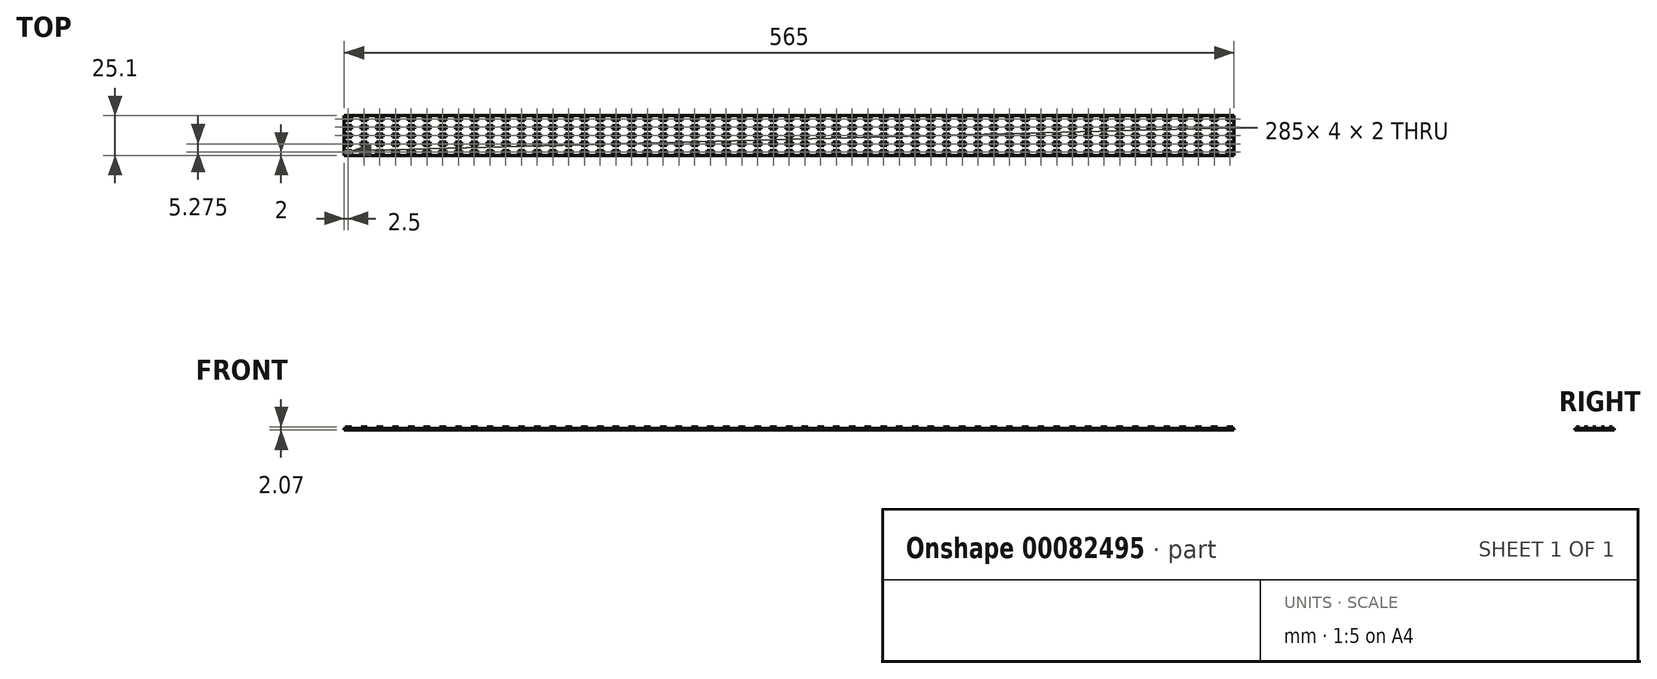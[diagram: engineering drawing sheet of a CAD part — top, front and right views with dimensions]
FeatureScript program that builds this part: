
annotation { "Feature Type Name" : "Feature", "Feature Type Description" : "" }
export const myFeature = defineFeature(function(context is Context, id is Id, definition is map)
    precondition{}
    {
        {
            var Q0;
            Q0=qCreatedBy(makeId("Right.planeOp"),FACE);
            var sketch = newSketch(context, id + "F0", { "sketchPlane" : qUnion([Q0])});
            skArc(sketch, "E0", {"start": v(-12.55, 0) * mm, "mid": v(0, -12.55) * mm, "end": v(12.55, 0) * mm});
            skLineSegment(sketch, "E1", {"start": v(-12.55, 0) * mm, "end": v(12.55, 0) * mm});
            skSolve(sketch);
        }
        {
            var Q0;
            Q0=qSketchRegion(id+"F0",true);
            extrude(context, id + "F1", {"entities" : qUnion([Q0]), "endBound" : BoundingType.SYMMETRIC, "depth" : 565 * mm});
        }
        {
            var Q0;
            Q0=makeQuery(id+"F1.opExtrude","SWEPT_FACE",FACE,{"disambiguationData":[OSD([sQuery(id+"F0.wireOp",EDGE,"E1")])]});
            var sketch = newSketch(context, id + "F2", { "sketchPlane" : qUnion([Q0])});
            skLineSegment(sketch, "E2.bottom", {"start": v(-282, 11.55) * mm, "end": v(-278, 11.55) * mm});
            skLineSegment(sketch, "E2.top", {"start": v(-282, 9.55) * mm, "end": v(-278, 9.55) * mm});
            skLineSegment(sketch, "E2.left", {"start": v(-282, 11.55) * mm, "end": v(-282, 9.55) * mm});
            skLineSegment(sketch, "E2.right", {"start": v(-278, 11.55) * mm, "end": v(-278, 9.55) * mm});
            skLineSegment(sketch, "E3.1.0.0", {"start": v(-282, 6.27) * mm, "end": v(-282, 4.27) * mm});
            skLineSegment(sketch, "E3.1.0.1", {"start": v(-282, 6.27) * mm, "end": v(-278, 6.27) * mm});
            skLineSegment(sketch, "E3.1.0.2", {"start": v(-278, 6.27) * mm, "end": v(-278, 4.27) * mm});
            skLineSegment(sketch, "E3.1.0.3", {"start": v(-282, 4.27) * mm, "end": v(-278, 4.27) * mm});
            skLineSegment(sketch, "E3.2.0.0", {"start": v(-282, 1) * mm, "end": v(-282, -1) * mm});
            skLineSegment(sketch, "E3.2.0.1", {"start": v(-282, 1) * mm, "end": v(-278, 1) * mm});
            skLineSegment(sketch, "E3.2.0.2", {"start": v(-278, 1) * mm, "end": v(-278, -1) * mm});
            skLineSegment(sketch, "E3.2.0.3", {"start": v(-282, -1) * mm, "end": v(-278, -1) * mm});
            skLineSegment(sketch, "E3.direction1", {"start": v(-278, 9.55) * mm, "end": v(-278, 4.27) * mm, "construction": true});
            skLineSegment(sketch, "E4.0.3.0", {"start": v(-282, -4.28) * mm, "end": v(-282, -6.28) * mm});
            skLineSegment(sketch, "E4.3.3.0", {"start": v(-282, -4.28) * mm, "end": v(-278, -4.28) * mm});
            skLineSegment(sketch, "E4.6.3.0", {"start": v(-278, -4.28) * mm, "end": v(-278, -6.28) * mm});
            skLineSegment(sketch, "E4.9.3.0", {"start": v(-282, -6.28) * mm, "end": v(-278, -6.28) * mm});
            skLineSegment(sketch, "E5.0.4.0", {"start": v(-282, -9.55) * mm, "end": v(-282, -11.55) * mm});
            skLineSegment(sketch, "E5.3.4.0", {"start": v(-282, -9.55) * mm, "end": v(-278, -9.55) * mm});
            skLineSegment(sketch, "E5.6.4.0", {"start": v(-278, -9.55) * mm, "end": v(-278, -11.55) * mm});
            skLineSegment(sketch, "E5.9.4.0", {"start": v(-282, -11.55) * mm, "end": v(-278, -11.55) * mm});
            skLineSegment(sketch, "E6.1.0.0", {"start": v(-272, -9.55) * mm, "end": v(-272, -11.55) * mm});
            skLineSegment(sketch, "E6.1.0.1", {"start": v(-268, -9.55) * mm, "end": v(-268, -11.55) * mm});
            skLineSegment(sketch, "E6.1.0.2", {"start": v(-272, -9.55) * mm, "end": v(-268, -9.55) * mm});
            skLineSegment(sketch, "E6.1.0.3", {"start": v(-268, 9.55) * mm, "end": v(-268, 4.27) * mm, "construction": true});
            skLineSegment(sketch, "E6.1.0.4", {"start": v(-272, -1) * mm, "end": v(-268, -1) * mm});
            skLineSegment(sketch, "E6.1.0.5", {"start": v(-272, -11.55) * mm, "end": v(-268, -11.55) * mm});
            skLineSegment(sketch, "E6.1.0.6", {"start": v(-268, 1) * mm, "end": v(-268, -1) * mm});
            skLineSegment(sketch, "E6.1.0.7", {"start": v(-272, 1) * mm, "end": v(-268, 1) * mm});
            skLineSegment(sketch, "E6.1.0.8", {"start": v(-272, 1) * mm, "end": v(-272, -1) * mm});
            skLineSegment(sketch, "E6.1.0.9", {"start": v(-272, 4.27) * mm, "end": v(-268, 4.27) * mm});
            skLineSegment(sketch, "E6.1.0.10", {"start": v(-268, 6.27) * mm, "end": v(-268, 4.27) * mm});
            skLineSegment(sketch, "E6.1.0.11", {"start": v(-272, 6.27) * mm, "end": v(-268, 6.27) * mm});
            skLineSegment(sketch, "E6.1.0.12", {"start": v(-272, 6.27) * mm, "end": v(-272, 4.27) * mm});
            skLineSegment(sketch, "E6.1.0.13", {"start": v(-268, 11.55) * mm, "end": v(-268, 9.55) * mm});
            skLineSegment(sketch, "E6.1.0.14", {"start": v(-272, 11.55) * mm, "end": v(-272, 9.55) * mm});
            skLineSegment(sketch, "E6.1.0.15", {"start": v(-272, 9.55) * mm, "end": v(-268, 9.55) * mm});
            skLineSegment(sketch, "E6.1.0.16", {"start": v(-272, -6.28) * mm, "end": v(-268, -6.28) * mm});
            skLineSegment(sketch, "E6.1.0.17", {"start": v(-272, 11.55) * mm, "end": v(-268, 11.55) * mm});
            skLineSegment(sketch, "E6.1.0.18", {"start": v(-268, -4.28) * mm, "end": v(-268, -6.28) * mm});
            skLineSegment(sketch, "E6.1.0.19", {"start": v(-272, -4.28) * mm, "end": v(-268, -4.28) * mm});
            skLineSegment(sketch, "E6.1.0.20", {"start": v(-272, -4.28) * mm, "end": v(-272, -6.28) * mm});
            skLineSegment(sketch, "E6.2.0.0", {"start": v(-262, -9.55) * mm, "end": v(-262, -11.55) * mm});
            skLineSegment(sketch, "E6.2.0.1", {"start": v(-258, -9.55) * mm, "end": v(-258, -11.55) * mm});
            skLineSegment(sketch, "E6.2.0.2", {"start": v(-262, -9.55) * mm, "end": v(-258, -9.55) * mm});
            skLineSegment(sketch, "E6.2.0.3", {"start": v(-258, 9.55) * mm, "end": v(-258, 4.27) * mm, "construction": true});
            skLineSegment(sketch, "E6.2.0.4", {"start": v(-262, -1) * mm, "end": v(-258, -1) * mm});
            skLineSegment(sketch, "E6.2.0.5", {"start": v(-262, -11.55) * mm, "end": v(-258, -11.55) * mm});
            skLineSegment(sketch, "E6.2.0.6", {"start": v(-258, 1) * mm, "end": v(-258, -1) * mm});
            skLineSegment(sketch, "E6.2.0.7", {"start": v(-262, 1) * mm, "end": v(-258, 1) * mm});
            skLineSegment(sketch, "E6.2.0.8", {"start": v(-262, 1) * mm, "end": v(-262, -1) * mm});
            skLineSegment(sketch, "E6.2.0.9", {"start": v(-262, 4.27) * mm, "end": v(-258, 4.27) * mm});
            skLineSegment(sketch, "E6.2.0.10", {"start": v(-258, 6.27) * mm, "end": v(-258, 4.27) * mm});
            skLineSegment(sketch, "E6.2.0.11", {"start": v(-262, 6.27) * mm, "end": v(-258, 6.27) * mm});
            skLineSegment(sketch, "E6.2.0.12", {"start": v(-262, 6.27) * mm, "end": v(-262, 4.27) * mm});
            skLineSegment(sketch, "E6.2.0.13", {"start": v(-258, 11.55) * mm, "end": v(-258, 9.55) * mm});
            skLineSegment(sketch, "E6.2.0.14", {"start": v(-262, 11.55) * mm, "end": v(-262, 9.55) * mm});
            skLineSegment(sketch, "E6.2.0.15", {"start": v(-262, 9.55) * mm, "end": v(-258, 9.55) * mm});
            skLineSegment(sketch, "E6.2.0.16", {"start": v(-262, -6.28) * mm, "end": v(-258, -6.28) * mm});
            skLineSegment(sketch, "E6.2.0.17", {"start": v(-262, 11.55) * mm, "end": v(-258, 11.55) * mm});
            skLineSegment(sketch, "E6.2.0.18", {"start": v(-258, -4.28) * mm, "end": v(-258, -6.28) * mm});
            skLineSegment(sketch, "E6.2.0.19", {"start": v(-262, -4.28) * mm, "end": v(-258, -4.28) * mm});
            skLineSegment(sketch, "E6.2.0.20", {"start": v(-262, -4.28) * mm, "end": v(-262, -6.28) * mm});
            skLineSegment(sketch, "E6.3.0.0", {"start": v(-252, -9.55) * mm, "end": v(-252, -11.55) * mm});
            skLineSegment(sketch, "E6.3.0.1", {"start": v(-248, -9.55) * mm, "end": v(-248, -11.55) * mm});
            skLineSegment(sketch, "E6.3.0.2", {"start": v(-252, -9.55) * mm, "end": v(-248, -9.55) * mm});
            skLineSegment(sketch, "E6.3.0.3", {"start": v(-248, 9.55) * mm, "end": v(-248, 4.27) * mm, "construction": true});
            skLineSegment(sketch, "E6.3.0.4", {"start": v(-252, -1) * mm, "end": v(-248, -1) * mm});
            skLineSegment(sketch, "E6.3.0.5", {"start": v(-252, -11.55) * mm, "end": v(-248, -11.55) * mm});
            skLineSegment(sketch, "E6.3.0.6", {"start": v(-248, 1) * mm, "end": v(-248, -1) * mm});
            skLineSegment(sketch, "E6.3.0.7", {"start": v(-252, 1) * mm, "end": v(-248, 1) * mm});
            skLineSegment(sketch, "E6.3.0.8", {"start": v(-252, 1) * mm, "end": v(-252, -1) * mm});
            skLineSegment(sketch, "E6.3.0.9", {"start": v(-252, 4.27) * mm, "end": v(-248, 4.27) * mm});
            skLineSegment(sketch, "E6.3.0.10", {"start": v(-248, 6.27) * mm, "end": v(-248, 4.27) * mm});
            skLineSegment(sketch, "E6.3.0.11", {"start": v(-252, 6.27) * mm, "end": v(-248, 6.27) * mm});
            skLineSegment(sketch, "E6.3.0.12", {"start": v(-252, 6.27) * mm, "end": v(-252, 4.27) * mm});
            skLineSegment(sketch, "E6.3.0.13", {"start": v(-248, 11.55) * mm, "end": v(-248, 9.55) * mm});
            skLineSegment(sketch, "E6.3.0.14", {"start": v(-252, 11.55) * mm, "end": v(-252, 9.55) * mm});
            skLineSegment(sketch, "E6.3.0.15", {"start": v(-252, 9.55) * mm, "end": v(-248, 9.55) * mm});
            skLineSegment(sketch, "E6.3.0.16", {"start": v(-252, -6.28) * mm, "end": v(-248, -6.28) * mm});
            skLineSegment(sketch, "E6.3.0.17", {"start": v(-252, 11.55) * mm, "end": v(-248, 11.55) * mm});
            skLineSegment(sketch, "E6.3.0.18", {"start": v(-248, -4.28) * mm, "end": v(-248, -6.28) * mm});
            skLineSegment(sketch, "E6.3.0.19", {"start": v(-252, -4.28) * mm, "end": v(-248, -4.28) * mm});
            skLineSegment(sketch, "E6.3.0.20", {"start": v(-252, -4.28) * mm, "end": v(-252, -6.28) * mm});
            skLineSegment(sketch, "E6.4.0.0", {"start": v(-242, -9.55) * mm, "end": v(-242, -11.55) * mm});
            skLineSegment(sketch, "E6.4.0.1", {"start": v(-238, -9.55) * mm, "end": v(-238, -11.55) * mm});
            skLineSegment(sketch, "E6.4.0.2", {"start": v(-242, -9.55) * mm, "end": v(-238, -9.55) * mm});
            skLineSegment(sketch, "E6.4.0.3", {"start": v(-238, 9.55) * mm, "end": v(-238, 4.27) * mm, "construction": true});
            skLineSegment(sketch, "E6.4.0.4", {"start": v(-242, -1) * mm, "end": v(-238, -1) * mm});
            skLineSegment(sketch, "E6.4.0.5", {"start": v(-242, -11.55) * mm, "end": v(-238, -11.55) * mm});
            skLineSegment(sketch, "E6.4.0.6", {"start": v(-238, 1) * mm, "end": v(-238, -1) * mm});
            skLineSegment(sketch, "E6.4.0.7", {"start": v(-242, 1) * mm, "end": v(-238, 1) * mm});
            skLineSegment(sketch, "E6.4.0.8", {"start": v(-242, 1) * mm, "end": v(-242, -1) * mm});
            skLineSegment(sketch, "E6.4.0.9", {"start": v(-242, 4.27) * mm, "end": v(-238, 4.27) * mm});
            skLineSegment(sketch, "E6.4.0.10", {"start": v(-238, 6.27) * mm, "end": v(-238, 4.27) * mm});
            skLineSegment(sketch, "E6.4.0.11", {"start": v(-242, 6.27) * mm, "end": v(-238, 6.27) * mm});
            skLineSegment(sketch, "E6.4.0.12", {"start": v(-242, 6.27) * mm, "end": v(-242, 4.27) * mm});
            skLineSegment(sketch, "E6.4.0.13", {"start": v(-238, 11.55) * mm, "end": v(-238, 9.55) * mm});
            skLineSegment(sketch, "E6.4.0.14", {"start": v(-242, 11.55) * mm, "end": v(-242, 9.55) * mm});
            skLineSegment(sketch, "E6.4.0.15", {"start": v(-242, 9.55) * mm, "end": v(-238, 9.55) * mm});
            skLineSegment(sketch, "E6.4.0.16", {"start": v(-242, -6.28) * mm, "end": v(-238, -6.28) * mm});
            skLineSegment(sketch, "E6.4.0.17", {"start": v(-242, 11.55) * mm, "end": v(-238, 11.55) * mm});
            skLineSegment(sketch, "E6.4.0.18", {"start": v(-238, -4.28) * mm, "end": v(-238, -6.28) * mm});
            skLineSegment(sketch, "E6.4.0.19", {"start": v(-242, -4.28) * mm, "end": v(-238, -4.28) * mm});
            skLineSegment(sketch, "E6.4.0.20", {"start": v(-242, -4.28) * mm, "end": v(-242, -6.28) * mm});
            skLineSegment(sketch, "E6.5.0.0", {"start": v(-232, -9.55) * mm, "end": v(-232, -11.55) * mm});
            skLineSegment(sketch, "E6.5.0.1", {"start": v(-228, -9.55) * mm, "end": v(-228, -11.55) * mm});
            skLineSegment(sketch, "E6.5.0.2", {"start": v(-232, -9.55) * mm, "end": v(-228, -9.55) * mm});
            skLineSegment(sketch, "E6.5.0.3", {"start": v(-228, 9.55) * mm, "end": v(-228, 4.27) * mm, "construction": true});
            skLineSegment(sketch, "E6.5.0.4", {"start": v(-232, -1) * mm, "end": v(-228, -1) * mm});
            skLineSegment(sketch, "E6.5.0.5", {"start": v(-232, -11.55) * mm, "end": v(-228, -11.55) * mm});
            skLineSegment(sketch, "E6.5.0.6", {"start": v(-228, 1) * mm, "end": v(-228, -1) * mm});
            skLineSegment(sketch, "E6.5.0.7", {"start": v(-232, 1) * mm, "end": v(-228, 1) * mm});
            skLineSegment(sketch, "E6.5.0.8", {"start": v(-232, 1) * mm, "end": v(-232, -1) * mm});
            skLineSegment(sketch, "E6.5.0.9", {"start": v(-232, 4.27) * mm, "end": v(-228, 4.27) * mm});
            skLineSegment(sketch, "E6.5.0.10", {"start": v(-228, 6.27) * mm, "end": v(-228, 4.27) * mm});
            skLineSegment(sketch, "E6.5.0.11", {"start": v(-232, 6.27) * mm, "end": v(-228, 6.27) * mm});
            skLineSegment(sketch, "E6.5.0.12", {"start": v(-232, 6.27) * mm, "end": v(-232, 4.27) * mm});
            skLineSegment(sketch, "E6.5.0.13", {"start": v(-228, 11.55) * mm, "end": v(-228, 9.55) * mm});
            skLineSegment(sketch, "E6.5.0.14", {"start": v(-232, 11.55) * mm, "end": v(-232, 9.55) * mm});
            skLineSegment(sketch, "E6.5.0.15", {"start": v(-232, 9.55) * mm, "end": v(-228, 9.55) * mm});
            skLineSegment(sketch, "E6.5.0.16", {"start": v(-232, -6.28) * mm, "end": v(-228, -6.28) * mm});
            skLineSegment(sketch, "E6.5.0.17", {"start": v(-232, 11.55) * mm, "end": v(-228, 11.55) * mm});
            skLineSegment(sketch, "E6.5.0.18", {"start": v(-228, -4.28) * mm, "end": v(-228, -6.28) * mm});
            skLineSegment(sketch, "E6.5.0.19", {"start": v(-232, -4.28) * mm, "end": v(-228, -4.28) * mm});
            skLineSegment(sketch, "E6.5.0.20", {"start": v(-232, -4.28) * mm, "end": v(-232, -6.28) * mm});
            skLineSegment(sketch, "E6.6.0.0", {"start": v(-222, -9.55) * mm, "end": v(-222, -11.55) * mm});
            skLineSegment(sketch, "E6.6.0.1", {"start": v(-218, -9.55) * mm, "end": v(-218, -11.55) * mm});
            skLineSegment(sketch, "E6.6.0.2", {"start": v(-222, -9.55) * mm, "end": v(-218, -9.55) * mm});
            skLineSegment(sketch, "E6.6.0.3", {"start": v(-218, 9.55) * mm, "end": v(-218, 4.27) * mm, "construction": true});
            skLineSegment(sketch, "E6.6.0.4", {"start": v(-222, -1) * mm, "end": v(-218, -1) * mm});
            skLineSegment(sketch, "E6.6.0.5", {"start": v(-222, -11.55) * mm, "end": v(-218, -11.55) * mm});
            skLineSegment(sketch, "E6.6.0.6", {"start": v(-218, 1) * mm, "end": v(-218, -1) * mm});
            skLineSegment(sketch, "E6.6.0.7", {"start": v(-222, 1) * mm, "end": v(-218, 1) * mm});
            skLineSegment(sketch, "E6.6.0.8", {"start": v(-222, 1) * mm, "end": v(-222, -1) * mm});
            skLineSegment(sketch, "E6.6.0.9", {"start": v(-222, 4.27) * mm, "end": v(-218, 4.27) * mm});
            skLineSegment(sketch, "E6.6.0.10", {"start": v(-218, 6.27) * mm, "end": v(-218, 4.27) * mm});
            skLineSegment(sketch, "E6.6.0.11", {"start": v(-222, 6.27) * mm, "end": v(-218, 6.27) * mm});
            skLineSegment(sketch, "E6.6.0.12", {"start": v(-222, 6.27) * mm, "end": v(-222, 4.27) * mm});
            skLineSegment(sketch, "E6.6.0.13", {"start": v(-218, 11.55) * mm, "end": v(-218, 9.55) * mm});
            skLineSegment(sketch, "E6.6.0.14", {"start": v(-222, 11.55) * mm, "end": v(-222, 9.55) * mm});
            skLineSegment(sketch, "E6.6.0.15", {"start": v(-222, 9.55) * mm, "end": v(-218, 9.55) * mm});
            skLineSegment(sketch, "E6.6.0.16", {"start": v(-222, -6.28) * mm, "end": v(-218, -6.28) * mm});
            skLineSegment(sketch, "E6.6.0.17", {"start": v(-222, 11.55) * mm, "end": v(-218, 11.55) * mm});
            skLineSegment(sketch, "E6.6.0.18", {"start": v(-218, -4.28) * mm, "end": v(-218, -6.28) * mm});
            skLineSegment(sketch, "E6.6.0.19", {"start": v(-222, -4.28) * mm, "end": v(-218, -4.28) * mm});
            skLineSegment(sketch, "E6.6.0.20", {"start": v(-222, -4.28) * mm, "end": v(-222, -6.28) * mm});
            skLineSegment(sketch, "E6.7.0.0", {"start": v(-212, -9.55) * mm, "end": v(-212, -11.55) * mm});
            skLineSegment(sketch, "E6.7.0.1", {"start": v(-208, -9.55) * mm, "end": v(-208, -11.55) * mm});
            skLineSegment(sketch, "E6.7.0.2", {"start": v(-212, -9.55) * mm, "end": v(-208, -9.55) * mm});
            skLineSegment(sketch, "E6.7.0.3", {"start": v(-208, 9.55) * mm, "end": v(-208, 4.27) * mm, "construction": true});
            skLineSegment(sketch, "E6.7.0.4", {"start": v(-212, -1) * mm, "end": v(-208, -1) * mm});
            skLineSegment(sketch, "E6.7.0.5", {"start": v(-212, -11.55) * mm, "end": v(-208, -11.55) * mm});
            skLineSegment(sketch, "E6.7.0.6", {"start": v(-208, 1) * mm, "end": v(-208, -1) * mm});
            skLineSegment(sketch, "E6.7.0.7", {"start": v(-212, 1) * mm, "end": v(-208, 1) * mm});
            skLineSegment(sketch, "E6.7.0.8", {"start": v(-212, 1) * mm, "end": v(-212, -1) * mm});
            skLineSegment(sketch, "E6.7.0.9", {"start": v(-212, 4.27) * mm, "end": v(-208, 4.27) * mm});
            skLineSegment(sketch, "E6.7.0.10", {"start": v(-208, 6.27) * mm, "end": v(-208, 4.27) * mm});
            skLineSegment(sketch, "E6.7.0.11", {"start": v(-212, 6.27) * mm, "end": v(-208, 6.27) * mm});
            skLineSegment(sketch, "E6.7.0.12", {"start": v(-212, 6.27) * mm, "end": v(-212, 4.27) * mm});
            skLineSegment(sketch, "E6.7.0.13", {"start": v(-208, 11.55) * mm, "end": v(-208, 9.55) * mm});
            skLineSegment(sketch, "E6.7.0.14", {"start": v(-212, 11.55) * mm, "end": v(-212, 9.55) * mm});
            skLineSegment(sketch, "E6.7.0.15", {"start": v(-212, 9.55) * mm, "end": v(-208, 9.55) * mm});
            skLineSegment(sketch, "E6.7.0.16", {"start": v(-212, -6.28) * mm, "end": v(-208, -6.28) * mm});
            skLineSegment(sketch, "E6.7.0.17", {"start": v(-212, 11.55) * mm, "end": v(-208, 11.55) * mm});
            skLineSegment(sketch, "E6.7.0.18", {"start": v(-208, -4.28) * mm, "end": v(-208, -6.28) * mm});
            skLineSegment(sketch, "E6.7.0.19", {"start": v(-212, -4.28) * mm, "end": v(-208, -4.28) * mm});
            skLineSegment(sketch, "E6.7.0.20", {"start": v(-212, -4.28) * mm, "end": v(-212, -6.28) * mm});
            skLineSegment(sketch, "E6.8.0.0", {"start": v(-202, -9.55) * mm, "end": v(-202, -11.55) * mm});
            skLineSegment(sketch, "E6.8.0.1", {"start": v(-198, -9.55) * mm, "end": v(-198, -11.55) * mm});
            skLineSegment(sketch, "E6.8.0.2", {"start": v(-202, -9.55) * mm, "end": v(-198, -9.55) * mm});
            skLineSegment(sketch, "E6.8.0.3", {"start": v(-198, 9.55) * mm, "end": v(-198, 4.27) * mm, "construction": true});
            skLineSegment(sketch, "E6.8.0.4", {"start": v(-202, -1) * mm, "end": v(-198, -1) * mm});
            skLineSegment(sketch, "E6.8.0.5", {"start": v(-202, -11.55) * mm, "end": v(-198, -11.55) * mm});
            skLineSegment(sketch, "E6.8.0.6", {"start": v(-198, 1) * mm, "end": v(-198, -1) * mm});
            skLineSegment(sketch, "E6.8.0.7", {"start": v(-202, 1) * mm, "end": v(-198, 1) * mm});
            skLineSegment(sketch, "E6.8.0.8", {"start": v(-202, 1) * mm, "end": v(-202, -1) * mm});
            skLineSegment(sketch, "E6.8.0.9", {"start": v(-202, 4.27) * mm, "end": v(-198, 4.27) * mm});
            skLineSegment(sketch, "E6.8.0.10", {"start": v(-198, 6.27) * mm, "end": v(-198, 4.27) * mm});
            skLineSegment(sketch, "E6.8.0.11", {"start": v(-202, 6.27) * mm, "end": v(-198, 6.27) * mm});
            skLineSegment(sketch, "E6.8.0.12", {"start": v(-202, 6.27) * mm, "end": v(-202, 4.27) * mm});
            skLineSegment(sketch, "E6.8.0.13", {"start": v(-198, 11.55) * mm, "end": v(-198, 9.55) * mm});
            skLineSegment(sketch, "E6.8.0.14", {"start": v(-202, 11.55) * mm, "end": v(-202, 9.55) * mm});
            skLineSegment(sketch, "E6.8.0.15", {"start": v(-202, 9.55) * mm, "end": v(-198, 9.55) * mm});
            skLineSegment(sketch, "E6.8.0.16", {"start": v(-202, -6.28) * mm, "end": v(-198, -6.28) * mm});
            skLineSegment(sketch, "E6.8.0.17", {"start": v(-202, 11.55) * mm, "end": v(-198, 11.55) * mm});
            skLineSegment(sketch, "E6.8.0.18", {"start": v(-198, -4.28) * mm, "end": v(-198, -6.28) * mm});
            skLineSegment(sketch, "E6.8.0.19", {"start": v(-202, -4.28) * mm, "end": v(-198, -4.28) * mm});
            skLineSegment(sketch, "E6.8.0.20", {"start": v(-202, -4.28) * mm, "end": v(-202, -6.28) * mm});
            skLineSegment(sketch, "E6.9.0.0", {"start": v(-192, -9.55) * mm, "end": v(-192, -11.55) * mm});
            skLineSegment(sketch, "E6.9.0.1", {"start": v(-188, -9.55) * mm, "end": v(-188, -11.55) * mm});
            skLineSegment(sketch, "E6.9.0.2", {"start": v(-192, -9.55) * mm, "end": v(-188, -9.55) * mm});
            skLineSegment(sketch, "E6.9.0.3", {"start": v(-188, 9.55) * mm, "end": v(-188, 4.27) * mm, "construction": true});
            skLineSegment(sketch, "E6.9.0.4", {"start": v(-192, -1) * mm, "end": v(-188, -1) * mm});
            skLineSegment(sketch, "E6.9.0.5", {"start": v(-192, -11.55) * mm, "end": v(-188, -11.55) * mm});
            skLineSegment(sketch, "E6.9.0.6", {"start": v(-188, 1) * mm, "end": v(-188, -1) * mm});
            skLineSegment(sketch, "E6.9.0.7", {"start": v(-192, 1) * mm, "end": v(-188, 1) * mm});
            skLineSegment(sketch, "E6.9.0.8", {"start": v(-192, 1) * mm, "end": v(-192, -1) * mm});
            skLineSegment(sketch, "E6.9.0.9", {"start": v(-192, 4.27) * mm, "end": v(-188, 4.27) * mm});
            skLineSegment(sketch, "E6.9.0.10", {"start": v(-188, 6.27) * mm, "end": v(-188, 4.27) * mm});
            skLineSegment(sketch, "E6.9.0.11", {"start": v(-192, 6.27) * mm, "end": v(-188, 6.27) * mm});
            skLineSegment(sketch, "E6.9.0.12", {"start": v(-192, 6.27) * mm, "end": v(-192, 4.27) * mm});
            skLineSegment(sketch, "E6.9.0.13", {"start": v(-188, 11.55) * mm, "end": v(-188, 9.55) * mm});
            skLineSegment(sketch, "E6.9.0.14", {"start": v(-192, 11.55) * mm, "end": v(-192, 9.55) * mm});
            skLineSegment(sketch, "E6.9.0.15", {"start": v(-192, 9.55) * mm, "end": v(-188, 9.55) * mm});
            skLineSegment(sketch, "E6.9.0.16", {"start": v(-192, -6.28) * mm, "end": v(-188, -6.28) * mm});
            skLineSegment(sketch, "E6.9.0.17", {"start": v(-192, 11.55) * mm, "end": v(-188, 11.55) * mm});
            skLineSegment(sketch, "E6.9.0.18", {"start": v(-188, -4.28) * mm, "end": v(-188, -6.28) * mm});
            skLineSegment(sketch, "E6.9.0.19", {"start": v(-192, -4.28) * mm, "end": v(-188, -4.28) * mm});
            skLineSegment(sketch, "E6.9.0.20", {"start": v(-192, -4.28) * mm, "end": v(-192, -6.28) * mm});
            skLineSegment(sketch, "E6.direction1", {"start": v(-282, -11.55) * mm, "end": v(-272, -11.55) * mm, "construction": true});
            skLineSegment(sketch, "E7.1.0.0", {"start": v(-172, -9.55) * mm, "end": v(-168, -9.55) * mm});
            skLineSegment(sketch, "E7.1.0.1", {"start": v(-168, -9.55) * mm, "end": v(-168, -11.55) * mm});
            skLineSegment(sketch, "E7.1.0.2", {"start": v(-102, 11.55) * mm, "end": v(-102, 9.55) * mm});
            skLineSegment(sketch, "E7.1.0.3", {"start": v(-112, -1) * mm, "end": v(-108, -1) * mm});
            skLineSegment(sketch, "E7.1.0.4", {"start": v(-132, 11.55) * mm, "end": v(-132, 9.55) * mm});
            skLineSegment(sketch, "E7.1.0.5", {"start": v(-102, 9.55) * mm, "end": v(-98, 9.55) * mm});
            skLineSegment(sketch, "E7.1.0.6", {"start": v(-162, 11.55) * mm, "end": v(-162, 9.55) * mm});
            skLineSegment(sketch, "E7.1.0.7", {"start": v(-132, 9.55) * mm, "end": v(-128, 9.55) * mm});
            skLineSegment(sketch, "E7.1.0.8", {"start": v(-102, -9.55) * mm, "end": v(-102, -11.55) * mm});
            skLineSegment(sketch, "E7.1.0.9", {"start": v(-162, 9.55) * mm, "end": v(-158, 9.55) * mm});
            skLineSegment(sketch, "E7.1.0.10", {"start": v(-108, 1) * mm, "end": v(-108, -1) * mm});
            skLineSegment(sketch, "E7.1.0.11", {"start": v(-92, 6.27) * mm, "end": v(-92, 4.27) * mm});
            skLineSegment(sketch, "E7.1.0.12", {"start": v(-102, 11.55) * mm, "end": v(-98, 11.55) * mm});
            skLineSegment(sketch, "E7.1.0.13", {"start": v(-98, -9.55) * mm, "end": v(-98, -11.55) * mm});
            skLineSegment(sketch, "E7.1.0.14", {"start": v(-172, -11.55) * mm, "end": v(-168, -11.55) * mm});
            skLineSegment(sketch, "E7.1.0.15", {"start": v(-112, 1) * mm, "end": v(-108, 1) * mm});
            skLineSegment(sketch, "E7.1.0.16", {"start": v(-132, 11.55) * mm, "end": v(-128, 11.55) * mm});
            skLineSegment(sketch, "E7.1.0.17", {"start": v(-128, -9.55) * mm, "end": v(-128, -11.55) * mm});
            skLineSegment(sketch, "E7.1.0.18", {"start": v(-102, -9.55) * mm, "end": v(-98, -9.55) * mm});
            skLineSegment(sketch, "E7.1.0.19", {"start": v(-162, 11.55) * mm, "end": v(-158, 11.55) * mm});
            skLineSegment(sketch, "E7.1.0.20", {"start": v(-132, -9.55) * mm, "end": v(-128, -9.55) * mm});
            skLineSegment(sketch, "E7.1.0.21", {"start": v(-132, -1) * mm, "end": v(-128, -1) * mm});
            skLineSegment(sketch, "E7.1.0.22", {"start": v(-102, -11.55) * mm, "end": v(-98, -11.55) * mm});
            skLineSegment(sketch, "E7.1.0.23", {"start": v(-162, -1) * mm, "end": v(-158, -1) * mm});
            skLineSegment(sketch, "E7.1.0.24", {"start": v(-132, -11.55) * mm, "end": v(-128, -11.55) * mm});
            skLineSegment(sketch, "E7.1.0.25", {"start": v(-122, -9.55) * mm, "end": v(-122, -11.55) * mm});
            skLineSegment(sketch, "E7.1.0.26", {"start": v(-88, -9.55) * mm, "end": v(-88, -11.55) * mm});
            skLineSegment(sketch, "E7.1.0.27", {"start": v(-128, 1) * mm, "end": v(-128, -1) * mm});
            skLineSegment(sketch, "E7.1.0.28", {"start": v(-152, -9.55) * mm, "end": v(-152, -11.55) * mm});
            skLineSegment(sketch, "E7.1.0.29", {"start": v(-118, -9.55) * mm, "end": v(-118, -11.55) * mm});
            skLineSegment(sketch, "E7.1.0.30", {"start": v(-92, -9.55) * mm, "end": v(-88, -9.55) * mm});
            skLineSegment(sketch, "E7.1.0.31", {"start": v(-132, 1) * mm, "end": v(-128, 1) * mm});
            skLineSegment(sketch, "E7.1.0.32", {"start": v(-148, -9.55) * mm, "end": v(-148, -11.55) * mm});
            skLineSegment(sketch, "E7.1.0.33", {"start": v(-122, -9.55) * mm, "end": v(-118, -9.55) * mm});
            skLineSegment(sketch, "E7.1.0.34", {"start": v(-152, -9.55) * mm, "end": v(-148, -9.55) * mm});
            skLineSegment(sketch, "E7.1.0.35", {"start": v(-112, 11.55) * mm, "end": v(-112, 9.55) * mm});
            skLineSegment(sketch, "E7.1.0.36", {"start": v(-172, 6.27) * mm, "end": v(-172, 4.27) * mm});
            skLineSegment(sketch, "E7.1.0.37", {"start": v(-112, 9.55) * mm, "end": v(-108, 9.55) * mm});
            skLineSegment(sketch, "E7.1.0.38", {"start": v(-92, -11.55) * mm, "end": v(-88, -11.55) * mm});
            skLineSegment(sketch, "E7.1.0.39", {"start": v(-162, 1) * mm, "end": v(-162, -1) * mm});
            skLineSegment(sketch, "E7.1.0.40", {"start": v(-122, -11.55) * mm, "end": v(-118, -11.55) * mm});
            skLineSegment(sketch, "E7.1.0.41", {"start": v(-182, 11.55) * mm, "end": v(-178, 11.55) * mm});
            skLineSegment(sketch, "E7.1.0.42", {"start": v(-182, 9.55) * mm, "end": v(-178, 9.55) * mm});
            skLineSegment(sketch, "E7.1.0.43", {"start": v(-182, 11.55) * mm, "end": v(-182, 9.55) * mm});
            skLineSegment(sketch, "E7.1.0.44", {"start": v(-182, 6.27) * mm, "end": v(-182, 4.27) * mm});
            skLineSegment(sketch, "E7.1.0.45", {"start": v(-182, 6.27) * mm, "end": v(-178, 6.27) * mm});
            skLineSegment(sketch, "E7.1.0.46", {"start": v(-182, 4.27) * mm, "end": v(-178, 4.27) * mm});
            skLineSegment(sketch, "E7.1.0.47", {"start": v(-152, -11.55) * mm, "end": v(-148, -11.55) * mm});
            skLineSegment(sketch, "E7.1.0.48", {"start": v(-112, 11.55) * mm, "end": v(-108, 11.55) * mm});
            skLineSegment(sketch, "E7.1.0.49", {"start": v(-162, 6.27) * mm, "end": v(-162, 4.27) * mm});
            skLineSegment(sketch, "E7.1.0.50", {"start": v(-172, 11.55) * mm, "end": v(-168, 11.55) * mm});
            skLineSegment(sketch, "E7.1.0.51", {"start": v(-128, 11.55) * mm, "end": v(-128, 9.55) * mm});
            skLineSegment(sketch, "E7.1.0.52", {"start": v(-138, -4.28) * mm, "end": v(-138, -6.28) * mm});
            skLineSegment(sketch, "E7.1.0.53", {"start": v(-142, -9.55) * mm, "end": v(-138, -9.55) * mm});
            skLineSegment(sketch, "E7.1.0.54", {"start": v(-152, 1) * mm, "end": v(-148, 1) * mm});
            skLineSegment(sketch, "E7.1.0.55", {"start": v(-112, -4.28) * mm, "end": v(-108, -4.28) * mm});
            skLineSegment(sketch, "E7.1.0.56", {"start": v(-92, 4.27) * mm, "end": v(-88, 4.27) * mm});
            skLineSegment(sketch, "E7.1.0.57", {"start": v(-138, 9.55) * mm, "end": v(-138, 4.27) * mm, "construction": true});
            skLineSegment(sketch, "E7.1.0.58", {"start": v(-152, 1) * mm, "end": v(-152, -1) * mm});
            skLineSegment(sketch, "E7.1.0.59", {"start": v(-158, 11.55) * mm, "end": v(-158, 9.55) * mm});
            skLineSegment(sketch, "E7.1.0.60", {"start": v(-168, -4.28) * mm, "end": v(-168, -6.28) * mm});
            skLineSegment(sketch, "E7.1.0.61", {"start": v(-122, 4.27) * mm, "end": v(-118, 4.27) * mm});
            skLineSegment(sketch, "E7.1.0.62", {"start": v(-142, -4.28) * mm, "end": v(-138, -4.28) * mm});
            skLineSegment(sketch, "E7.1.0.63", {"start": v(-88, 6.27) * mm, "end": v(-88, 4.27) * mm});
            skLineSegment(sketch, "E7.1.0.64", {"start": v(-112, -4.28) * mm, "end": v(-112, -6.28) * mm});
            skLineSegment(sketch, "E7.1.0.65", {"start": v(-168, 9.55) * mm, "end": v(-168, 4.27) * mm, "construction": true});
            skLineSegment(sketch, "E7.1.0.66", {"start": v(-142, -1) * mm, "end": v(-138, -1) * mm});
            skLineSegment(sketch, "E7.1.0.67", {"start": v(-152, 4.27) * mm, "end": v(-148, 4.27) * mm});
            skLineSegment(sketch, "E7.1.0.68", {"start": v(-172, -4.28) * mm, "end": v(-168, -4.28) * mm});
            skLineSegment(sketch, "E7.1.0.69", {"start": v(-112, -11.55) * mm, "end": v(-108, -11.55) * mm});
            skLineSegment(sketch, "E7.1.0.70", {"start": v(-118, 6.27) * mm, "end": v(-118, 4.27) * mm});
            skLineSegment(sketch, "E7.1.0.71", {"start": v(-92, 6.27) * mm, "end": v(-88, 6.27) * mm});
            skLineSegment(sketch, "E7.1.0.72", {"start": v(-102, -6.28) * mm, "end": v(-98, -6.28) * mm});
            skLineSegment(sketch, "E7.1.0.73", {"start": v(-142, -11.55) * mm, "end": v(-138, -11.55) * mm});
            skLineSegment(sketch, "E7.1.0.74", {"start": v(-148, 6.27) * mm, "end": v(-148, 4.27) * mm});
            skLineSegment(sketch, "E7.1.0.75", {"start": v(-122, 6.27) * mm, "end": v(-118, 6.27) * mm});
            skLineSegment(sketch, "E7.1.0.76", {"start": v(-132, -6.28) * mm, "end": v(-128, -6.28) * mm});
            skLineSegment(sketch, "E7.1.0.77", {"start": v(-132, -9.55) * mm, "end": v(-132, -11.55) * mm});
            skLineSegment(sketch, "E7.1.0.78", {"start": v(-138, 1) * mm, "end": v(-138, -1) * mm});
            skLineSegment(sketch, "E7.1.0.79", {"start": v(-152, 6.27) * mm, "end": v(-148, 6.27) * mm});
            skLineSegment(sketch, "E7.1.0.80", {"start": v(-162, -6.28) * mm, "end": v(-158, -6.28) * mm});
            skLineSegment(sketch, "E7.1.0.81", {"start": v(-162, -9.55) * mm, "end": v(-162, -11.55) * mm});
            skLineSegment(sketch, "E7.1.0.82", {"start": v(-122, 6.27) * mm, "end": v(-122, 4.27) * mm});
            skLineSegment(sketch, "E7.1.0.83", {"start": v(-88, 11.55) * mm, "end": v(-88, 9.55) * mm});
            skLineSegment(sketch, "E7.1.0.84", {"start": v(-98, -4.28) * mm, "end": v(-98, -6.28) * mm});
            skLineSegment(sketch, "E7.1.0.85", {"start": v(-142, 1) * mm, "end": v(-138, 1) * mm});
            skLineSegment(sketch, "E7.1.0.86", {"start": v(-152, 6.27) * mm, "end": v(-152, 4.27) * mm});
            skLineSegment(sketch, "E7.1.0.87", {"start": v(-158, -9.55) * mm, "end": v(-158, -11.55) * mm});
            skLineSegment(sketch, "E7.1.0.88", {"start": v(-112, 1) * mm, "end": v(-112, -1) * mm});
            skLineSegment(sketch, "E7.1.0.89", {"start": v(-118, 11.55) * mm, "end": v(-118, 9.55) * mm});
            skLineSegment(sketch, "E7.1.0.90", {"start": v(-128, -4.28) * mm, "end": v(-128, -6.28) * mm});
            skLineSegment(sketch, "E7.1.0.91", {"start": v(-92, 11.55) * mm, "end": v(-92, 9.55) * mm});
            skLineSegment(sketch, "E7.1.0.92", {"start": v(-102, -4.28) * mm, "end": v(-98, -4.28) * mm});
            skLineSegment(sketch, "E7.1.0.93", {"start": v(-142, 4.27) * mm, "end": v(-138, 4.27) * mm});
            skLineSegment(sketch, "E7.1.0.94", {"start": v(-152, 11.55) * mm, "end": v(-152, 9.55) * mm});
            skLineSegment(sketch, "E7.1.0.95", {"start": v(-162, -4.28) * mm, "end": v(-158, -4.28) * mm});
            skLineSegment(sketch, "E7.1.0.96", {"start": v(-122, 9.55) * mm, "end": v(-118, 9.55) * mm});
            skLineSegment(sketch, "E7.1.0.97", {"start": v(-92, -6.28) * mm, "end": v(-88, -6.28) * mm});
            skLineSegment(sketch, "E7.1.0.98", {"start": v(-92, -9.55) * mm, "end": v(-92, -11.55) * mm});
            skLineSegment(sketch, "E7.1.0.99", {"start": v(-148, 11.55) * mm, "end": v(-148, 9.55) * mm});
            skLineSegment(sketch, "E7.1.0.100", {"start": v(-162, -9.55) * mm, "end": v(-158, -9.55) * mm});
            skLineSegment(sketch, "E7.1.0.101", {"start": v(-112, 4.27) * mm, "end": v(-108, 4.27) * mm});
            skLineSegment(sketch, "E7.1.0.102", {"start": v(-122, 11.55) * mm, "end": v(-122, 9.55) * mm});
            skLineSegment(sketch, "E7.1.0.103", {"start": v(-132, -4.28) * mm, "end": v(-128, -4.28) * mm});
            skLineSegment(sketch, "E7.1.0.104", {"start": v(-92, 9.55) * mm, "end": v(-88, 9.55) * mm});
            skLineSegment(sketch, "E7.1.0.105", {"start": v(-102, -1) * mm, "end": v(-98, -1) * mm});
            skLineSegment(sketch, "E7.1.0.106", {"start": v(-172, 4.27) * mm, "end": v(-168, 4.27) * mm});
            skLineSegment(sketch, "E7.1.0.107", {"start": v(-138, 6.27) * mm, "end": v(-138, 4.27) * mm});
            skLineSegment(sketch, "E7.1.0.108", {"start": v(-152, 9.55) * mm, "end": v(-148, 9.55) * mm});
            skLineSegment(sketch, "E7.1.0.109", {"start": v(-162, -4.28) * mm, "end": v(-162, -6.28) * mm});
            skLineSegment(sketch, "E7.1.0.110", {"start": v(-98, 1) * mm, "end": v(-98, -1) * mm});
            skLineSegment(sketch, "E7.1.0.111", {"start": v(-112, 6.27) * mm, "end": v(-108, 6.27) * mm});
            skLineSegment(sketch, "E7.1.0.112", {"start": v(-122, -6.28) * mm, "end": v(-118, -6.28) * mm});
            skLineSegment(sketch, "E7.1.0.113", {"start": v(-92, 11.55) * mm, "end": v(-88, 11.55) * mm});
            skLineSegment(sketch, "E7.1.0.114", {"start": v(-162, -11.55) * mm, "end": v(-158, -11.55) * mm});
            skLineSegment(sketch, "E7.1.0.115", {"start": v(-168, 6.27) * mm, "end": v(-168, 4.27) * mm});
            skLineSegment(sketch, "E7.1.0.116", {"start": v(-142, 6.27) * mm, "end": v(-138, 6.27) * mm});
            skLineSegment(sketch, "E7.1.0.117", {"start": v(-152, -6.28) * mm, "end": v(-148, -6.28) * mm});
            skLineSegment(sketch, "E7.1.0.118", {"start": v(-102, 1) * mm, "end": v(-98, 1) * mm});
            skLineSegment(sketch, "E7.1.0.119", {"start": v(-112, 6.27) * mm, "end": v(-112, 4.27) * mm});
            skLineSegment(sketch, "E7.1.0.120", {"start": v(-122, 11.55) * mm, "end": v(-118, 11.55) * mm});
            skLineSegment(sketch, "E7.1.0.121", {"start": v(-88, -4.28) * mm, "end": v(-88, -6.28) * mm});
            skLineSegment(sketch, "E7.1.0.122", {"start": v(-158, 1) * mm, "end": v(-158, -1) * mm});
            skLineSegment(sketch, "E7.1.0.123", {"start": v(-172, 6.27) * mm, "end": v(-168, 6.27) * mm});
            skLineSegment(sketch, "E7.1.0.124", {"start": v(-182, -6.28) * mm, "end": v(-178, -6.28) * mm});
            skLineSegment(sketch, "E7.1.0.125", {"start": v(-142, 6.27) * mm, "end": v(-142, 4.27) * mm});
            skLineSegment(sketch, "E7.1.0.126", {"start": v(-152, 11.55) * mm, "end": v(-148, 11.55) * mm});
            skLineSegment(sketch, "E7.1.0.127", {"start": v(-102, 1) * mm, "end": v(-102, -1) * mm});
            skLineSegment(sketch, "E7.1.0.128", {"start": v(-108, 11.55) * mm, "end": v(-108, 9.55) * mm});
            skLineSegment(sketch, "E7.1.0.129", {"start": v(-118, -4.28) * mm, "end": v(-118, -6.28) * mm});
            skLineSegment(sketch, "E7.1.0.130", {"start": v(-92, -4.28) * mm, "end": v(-88, -4.28) * mm});
            skLineSegment(sketch, "E7.1.0.131", {"start": v(-88, 9.55) * mm, "end": v(-88, 4.27) * mm, "construction": true});
            skLineSegment(sketch, "E7.1.0.132", {"start": v(-132, 1) * mm, "end": v(-132, -1) * mm});
            skLineSegment(sketch, "E7.1.0.133", {"start": v(-138, 11.55) * mm, "end": v(-138, 9.55) * mm});
            skLineSegment(sketch, "E7.1.0.134", {"start": v(-148, -4.28) * mm, "end": v(-148, -6.28) * mm});
            skLineSegment(sketch, "E7.1.0.135", {"start": v(-122, -4.28) * mm, "end": v(-118, -4.28) * mm});
            skLineSegment(sketch, "E7.1.0.136", {"start": v(-118, 9.55) * mm, "end": v(-118, 4.27) * mm, "construction": true});
            skLineSegment(sketch, "E7.1.0.137", {"start": v(-92, -4.28) * mm, "end": v(-92, -6.28) * mm});
            skLineSegment(sketch, "E7.1.0.138", {"start": v(-162, 1) * mm, "end": v(-158, 1) * mm});
            skLineSegment(sketch, "E7.1.0.139", {"start": v(-182, -9.55) * mm, "end": v(-182, -11.55) * mm});
            skLineSegment(sketch, "E7.1.0.140", {"start": v(-122, -4.28) * mm, "end": v(-122, -6.28) * mm});
            skLineSegment(sketch, "E7.1.0.141", {"start": v(-182, -11.55) * mm, "end": v(-172, -11.55) * mm, "construction": true});
            skLineSegment(sketch, "E7.1.0.142", {"start": v(-168, 11.55) * mm, "end": v(-168, 9.55) * mm});
            skLineSegment(sketch, "E7.1.0.143", {"start": v(-182, -9.55) * mm, "end": v(-178, -9.55) * mm});
            skLineSegment(sketch, "E7.1.0.144", {"start": v(-142, 11.55) * mm, "end": v(-142, 9.55) * mm});
            skLineSegment(sketch, "E7.1.0.145", {"start": v(-152, -4.28) * mm, "end": v(-148, -4.28) * mm});
            skLineSegment(sketch, "E7.1.0.146", {"start": v(-148, 9.55) * mm, "end": v(-148, 4.27) * mm, "construction": true});
            skLineSegment(sketch, "E7.1.0.147", {"start": v(-162, 4.27) * mm, "end": v(-158, 4.27) * mm});
            skLineSegment(sketch, "E7.1.0.148", {"start": v(-172, 11.55) * mm, "end": v(-172, 9.55) * mm});
            skLineSegment(sketch, "E7.1.0.149", {"start": v(-178, -9.55) * mm, "end": v(-178, -11.55) * mm});
            skLineSegment(sketch, "E7.1.0.150", {"start": v(-142, 9.55) * mm, "end": v(-138, 9.55) * mm});
            skLineSegment(sketch, "E7.1.0.151", {"start": v(-152, -4.28) * mm, "end": v(-152, -6.28) * mm});
            skLineSegment(sketch, "E7.1.0.152", {"start": v(-152, -1) * mm, "end": v(-148, -1) * mm});
            skLineSegment(sketch, "E7.1.0.153", {"start": v(-112, -6.28) * mm, "end": v(-108, -6.28) * mm});
            skLineSegment(sketch, "E7.1.0.154", {"start": v(-112, -9.55) * mm, "end": v(-112, -11.55) * mm});
            skLineSegment(sketch, "E7.1.0.155", {"start": v(-182, -4.28) * mm, "end": v(-182, -6.28) * mm});
            skLineSegment(sketch, "E7.1.0.156", {"start": v(-182, -4.28) * mm, "end": v(-178, -4.28) * mm});
            skLineSegment(sketch, "E7.1.0.157", {"start": v(-178, -4.28) * mm, "end": v(-178, -6.28) * mm});
            skLineSegment(sketch, "E7.1.0.158", {"start": v(-178, 6.27) * mm, "end": v(-178, 4.27) * mm});
            skLineSegment(sketch, "E7.1.0.159", {"start": v(-182, 1) * mm, "end": v(-182, -1) * mm});
            skLineSegment(sketch, "E7.1.0.160", {"start": v(-182, 1) * mm, "end": v(-178, 1) * mm});
            skLineSegment(sketch, "E7.1.0.161", {"start": v(-172, 9.55) * mm, "end": v(-168, 9.55) * mm});
            skLineSegment(sketch, "E7.1.0.162", {"start": v(-182, -11.55) * mm, "end": v(-178, -11.55) * mm});
            skLineSegment(sketch, "E7.1.0.163", {"start": v(-182, -1) * mm, "end": v(-178, -1) * mm});
            skLineSegment(sketch, "E7.1.0.164", {"start": v(-142, -6.28) * mm, "end": v(-138, -6.28) * mm});
            skLineSegment(sketch, "E7.1.0.165", {"start": v(-142, -9.55) * mm, "end": v(-142, -11.55) * mm});
            skLineSegment(sketch, "E7.1.0.166", {"start": v(-108, -9.55) * mm, "end": v(-108, -11.55) * mm});
            skLineSegment(sketch, "E7.1.0.167", {"start": v(-162, 6.27) * mm, "end": v(-158, 6.27) * mm});
            skLineSegment(sketch, "E7.1.0.168", {"start": v(-172, -6.28) * mm, "end": v(-168, -6.28) * mm});
            skLineSegment(sketch, "E7.1.0.169", {"start": v(-172, -9.55) * mm, "end": v(-172, -11.55) * mm});
            skLineSegment(sketch, "E7.1.0.170", {"start": v(-142, 11.55) * mm, "end": v(-138, 11.55) * mm});
            skLineSegment(sketch, "E7.1.0.171", {"start": v(-138, -9.55) * mm, "end": v(-138, -11.55) * mm});
            skLineSegment(sketch, "E7.1.0.172", {"start": v(-148, 1) * mm, "end": v(-148, -1) * mm});
            skLineSegment(sketch, "E7.1.0.173", {"start": v(-112, -9.55) * mm, "end": v(-108, -9.55) * mm});
            skLineSegment(sketch, "E7.1.0.174", {"start": v(-108, 9.55) * mm, "end": v(-108, 4.27) * mm, "construction": true});
            skLineSegment(sketch, "E7.1.0.175", {"start": v(-122, 1) * mm, "end": v(-122, -1) * mm});
            skLineSegment(sketch, "E7.1.0.176", {"start": v(-142, -4.28) * mm, "end": v(-142, -6.28) * mm});
            skLineSegment(sketch, "E7.1.0.177", {"start": v(-172, -1) * mm, "end": v(-168, -1) * mm});
            skLineSegment(sketch, "E7.1.0.178", {"start": v(-172, -4.28) * mm, "end": v(-172, -6.28) * mm});
            skLineSegment(sketch, "E7.1.0.179", {"start": v(-168, 1) * mm, "end": v(-168, -1) * mm});
            skLineSegment(sketch, "E7.1.0.180", {"start": v(-98, 9.55) * mm, "end": v(-98, 4.27) * mm, "construction": true});
            skLineSegment(sketch, "E7.1.0.181", {"start": v(-158, 9.55) * mm, "end": v(-158, 4.27) * mm, "construction": true});
            skLineSegment(sketch, "E7.1.0.182", {"start": v(-172, 1) * mm, "end": v(-172, -1) * mm});
            skLineSegment(sketch, "E7.1.0.183", {"start": v(-108, 6.27) * mm, "end": v(-108, 4.27) * mm});
            skLineSegment(sketch, "E7.1.0.184", {"start": v(-132, -4.28) * mm, "end": v(-132, -6.28) * mm});
            skLineSegment(sketch, "E7.1.0.185", {"start": v(-172, 1) * mm, "end": v(-168, 1) * mm});
            skLineSegment(sketch, "E7.1.0.186", {"start": v(-142, 1) * mm, "end": v(-142, -1) * mm});
            skLineSegment(sketch, "E7.1.0.187", {"start": v(-158, -4.28) * mm, "end": v(-158, -6.28) * mm});
            skLineSegment(sketch, "E7.1.0.188", {"start": v(-128, 9.55) * mm, "end": v(-128, 4.27) * mm, "construction": true});
            skLineSegment(sketch, "E7.1.0.189", {"start": v(-102, -4.28) * mm, "end": v(-102, -6.28) * mm});
            skLineSegment(sketch, "E7.1.0.190", {"start": v(-102, 4.27) * mm, "end": v(-98, 4.27) * mm});
            skLineSegment(sketch, "E7.1.0.191", {"start": v(-92, -1) * mm, "end": v(-88, -1) * mm});
            skLineSegment(sketch, "E7.1.0.192", {"start": v(-98, 6.27) * mm, "end": v(-98, 4.27) * mm});
            skLineSegment(sketch, "E7.1.0.193", {"start": v(-122, -1) * mm, "end": v(-118, -1) * mm});
            skLineSegment(sketch, "E7.1.0.194", {"start": v(-132, 4.27) * mm, "end": v(-128, 4.27) * mm});
            skLineSegment(sketch, "E7.1.0.195", {"start": v(-88, 1) * mm, "end": v(-88, -1) * mm});
            skLineSegment(sketch, "E7.1.0.196", {"start": v(-128, 6.27) * mm, "end": v(-128, 4.27) * mm});
            skLineSegment(sketch, "E7.1.0.197", {"start": v(-102, 6.27) * mm, "end": v(-98, 6.27) * mm});
            skLineSegment(sketch, "E7.1.0.198", {"start": v(-178, 11.55) * mm, "end": v(-178, 9.55) * mm});
            skLineSegment(sketch, "E7.1.0.199", {"start": v(-178, 1) * mm, "end": v(-178, -1) * mm});
            skLineSegment(sketch, "E7.1.0.200", {"start": v(-158, 6.27) * mm, "end": v(-158, 4.27) * mm});
            skLineSegment(sketch, "E7.1.0.201", {"start": v(-132, 6.27) * mm, "end": v(-128, 6.27) * mm});
            skLineSegment(sketch, "E7.1.0.202", {"start": v(-178, 9.55) * mm, "end": v(-178, 4.27) * mm, "construction": true});
            skLineSegment(sketch, "E7.1.0.203", {"start": v(-102, 6.27) * mm, "end": v(-102, 4.27) * mm});
            skLineSegment(sketch, "E7.1.0.204", {"start": v(-118, 1) * mm, "end": v(-118, -1) * mm});
            skLineSegment(sketch, "E7.1.0.205", {"start": v(-92, 1) * mm, "end": v(-88, 1) * mm});
            skLineSegment(sketch, "E7.1.0.206", {"start": v(-132, 6.27) * mm, "end": v(-132, 4.27) * mm});
            skLineSegment(sketch, "E7.1.0.207", {"start": v(-98, 11.55) * mm, "end": v(-98, 9.55) * mm});
            skLineSegment(sketch, "E7.1.0.208", {"start": v(-108, -4.28) * mm, "end": v(-108, -6.28) * mm});
            skLineSegment(sketch, "E7.1.0.209", {"start": v(-122, 1) * mm, "end": v(-118, 1) * mm});
            skLineSegment(sketch, "E7.1.0.210", {"start": v(-92, 1) * mm, "end": v(-92, -1) * mm});
            skLineSegment(sketch, "E7.2.0.0", {"start": v(-72, -9.55) * mm, "end": v(-68, -9.55) * mm});
            skLineSegment(sketch, "E7.2.0.1", {"start": v(-68, -9.55) * mm, "end": v(-68, -11.55) * mm});
            skLineSegment(sketch, "E7.2.0.2", {"start": v(-2, 11.55) * mm, "end": v(-2, 9.55) * mm});
            skLineSegment(sketch, "E7.2.0.3", {"start": v(-12, -1) * mm, "end": v(-8, -1) * mm});
            skLineSegment(sketch, "E7.2.0.4", {"start": v(-32, 11.55) * mm, "end": v(-32, 9.55) * mm});
            skLineSegment(sketch, "E7.2.0.5", {"start": v(-2, 9.55) * mm, "end": v(2, 9.55) * mm});
            skLineSegment(sketch, "E7.2.0.6", {"start": v(-62, 11.55) * mm, "end": v(-62, 9.55) * mm});
            skLineSegment(sketch, "E7.2.0.7", {"start": v(-32, 9.55) * mm, "end": v(-28, 9.55) * mm});
            skLineSegment(sketch, "E7.2.0.8", {"start": v(-2, -9.55) * mm, "end": v(-2, -11.55) * mm});
            skLineSegment(sketch, "E7.2.0.9", {"start": v(-62, 9.55) * mm, "end": v(-58, 9.55) * mm});
            skLineSegment(sketch, "E7.2.0.10", {"start": v(-8, 1) * mm, "end": v(-8, -1) * mm});
            skLineSegment(sketch, "E7.2.0.11", {"start": v(8, 6.27) * mm, "end": v(8, 4.27) * mm});
            skLineSegment(sketch, "E7.2.0.12", {"start": v(-2, 11.55) * mm, "end": v(2, 11.55) * mm});
            skLineSegment(sketch, "E7.2.0.13", {"start": v(2, -9.55) * mm, "end": v(2, -11.55) * mm});
            skLineSegment(sketch, "E7.2.0.14", {"start": v(-72, -11.55) * mm, "end": v(-68, -11.55) * mm});
            skLineSegment(sketch, "E7.2.0.15", {"start": v(-12, 1) * mm, "end": v(-8, 1) * mm});
            skLineSegment(sketch, "E7.2.0.16", {"start": v(-32, 11.55) * mm, "end": v(-28, 11.55) * mm});
            skLineSegment(sketch, "E7.2.0.17", {"start": v(-28, -9.55) * mm, "end": v(-28, -11.55) * mm});
            skLineSegment(sketch, "E7.2.0.18", {"start": v(-2, -9.55) * mm, "end": v(2, -9.55) * mm});
            skLineSegment(sketch, "E7.2.0.19", {"start": v(-62, 11.55) * mm, "end": v(-58, 11.55) * mm});
            skLineSegment(sketch, "E7.2.0.20", {"start": v(-32, -9.55) * mm, "end": v(-28, -9.55) * mm});
            skLineSegment(sketch, "E7.2.0.21", {"start": v(-32, -1) * mm, "end": v(-28, -1) * mm});
            skLineSegment(sketch, "E7.2.0.22", {"start": v(-2, -11.55) * mm, "end": v(2, -11.55) * mm});
            skLineSegment(sketch, "E7.2.0.23", {"start": v(-62, -1) * mm, "end": v(-58, -1) * mm});
            skLineSegment(sketch, "E7.2.0.24", {"start": v(-32, -11.55) * mm, "end": v(-28, -11.55) * mm});
            skLineSegment(sketch, "E7.2.0.25", {"start": v(-22, -9.55) * mm, "end": v(-22, -11.55) * mm});
            skLineSegment(sketch, "E7.2.0.26", {"start": v(12, -9.55) * mm, "end": v(12, -11.55) * mm});
            skLineSegment(sketch, "E7.2.0.27", {"start": v(-28, 1) * mm, "end": v(-28, -1) * mm});
            skLineSegment(sketch, "E7.2.0.28", {"start": v(-52, -9.55) * mm, "end": v(-52, -11.55) * mm});
            skLineSegment(sketch, "E7.2.0.29", {"start": v(-18, -9.55) * mm, "end": v(-18, -11.55) * mm});
            skLineSegment(sketch, "E7.2.0.30", {"start": v(8, -9.55) * mm, "end": v(12, -9.55) * mm});
            skLineSegment(sketch, "E7.2.0.31", {"start": v(-32, 1) * mm, "end": v(-28, 1) * mm});
            skLineSegment(sketch, "E7.2.0.32", {"start": v(-48, -9.55) * mm, "end": v(-48, -11.55) * mm});
            skLineSegment(sketch, "E7.2.0.33", {"start": v(-22, -9.55) * mm, "end": v(-18, -9.55) * mm});
            skLineSegment(sketch, "E7.2.0.34", {"start": v(-52, -9.55) * mm, "end": v(-48, -9.55) * mm});
            skLineSegment(sketch, "E7.2.0.35", {"start": v(-12, 11.55) * mm, "end": v(-12, 9.55) * mm});
            skLineSegment(sketch, "E7.2.0.36", {"start": v(-72, 6.27) * mm, "end": v(-72, 4.27) * mm});
            skLineSegment(sketch, "E7.2.0.37", {"start": v(-12, 9.55) * mm, "end": v(-8, 9.55) * mm});
            skLineSegment(sketch, "E7.2.0.38", {"start": v(8, -11.55) * mm, "end": v(12, -11.55) * mm});
            skLineSegment(sketch, "E7.2.0.39", {"start": v(-62, 1) * mm, "end": v(-62, -1) * mm});
            skLineSegment(sketch, "E7.2.0.40", {"start": v(-22, -11.55) * mm, "end": v(-18, -11.55) * mm});
            skLineSegment(sketch, "E7.2.0.41", {"start": v(-82, 11.55) * mm, "end": v(-78, 11.55) * mm});
            skLineSegment(sketch, "E7.2.0.42", {"start": v(-82, 9.55) * mm, "end": v(-78, 9.55) * mm});
            skLineSegment(sketch, "E7.2.0.43", {"start": v(-82, 11.55) * mm, "end": v(-82, 9.55) * mm});
            skLineSegment(sketch, "E7.2.0.44", {"start": v(-82, 6.27) * mm, "end": v(-82, 4.27) * mm});
            skLineSegment(sketch, "E7.2.0.45", {"start": v(-82, 6.27) * mm, "end": v(-78, 6.27) * mm});
            skLineSegment(sketch, "E7.2.0.46", {"start": v(-82, 4.27) * mm, "end": v(-78, 4.27) * mm});
            skLineSegment(sketch, "E7.2.0.47", {"start": v(-52, -11.55) * mm, "end": v(-48, -11.55) * mm});
            skLineSegment(sketch, "E7.2.0.48", {"start": v(-12, 11.55) * mm, "end": v(-8, 11.55) * mm});
            skLineSegment(sketch, "E7.2.0.49", {"start": v(-62, 6.27) * mm, "end": v(-62, 4.27) * mm});
            skLineSegment(sketch, "E7.2.0.50", {"start": v(-72, 11.55) * mm, "end": v(-68, 11.55) * mm});
            skLineSegment(sketch, "E7.2.0.51", {"start": v(-28, 11.55) * mm, "end": v(-28, 9.55) * mm});
            skLineSegment(sketch, "E7.2.0.52", {"start": v(-38, -4.28) * mm, "end": v(-38, -6.28) * mm});
            skLineSegment(sketch, "E7.2.0.53", {"start": v(-42, -9.55) * mm, "end": v(-38, -9.55) * mm});
            skLineSegment(sketch, "E7.2.0.54", {"start": v(-52, 1) * mm, "end": v(-48, 1) * mm});
            skLineSegment(sketch, "E7.2.0.55", {"start": v(-12, -4.28) * mm, "end": v(-8, -4.28) * mm});
            skLineSegment(sketch, "E7.2.0.56", {"start": v(8, 4.27) * mm, "end": v(12, 4.27) * mm});
            skLineSegment(sketch, "E7.2.0.57", {"start": v(-38, 9.55) * mm, "end": v(-38, 4.27) * mm, "construction": true});
            skLineSegment(sketch, "E7.2.0.58", {"start": v(-52, 1) * mm, "end": v(-52, -1) * mm});
            skLineSegment(sketch, "E7.2.0.59", {"start": v(-58, 11.55) * mm, "end": v(-58, 9.55) * mm});
            skLineSegment(sketch, "E7.2.0.60", {"start": v(-68, -4.28) * mm, "end": v(-68, -6.28) * mm});
            skLineSegment(sketch, "E7.2.0.61", {"start": v(-22, 4.27) * mm, "end": v(-18, 4.27) * mm});
            skLineSegment(sketch, "E7.2.0.62", {"start": v(-42, -4.28) * mm, "end": v(-38, -4.28) * mm});
            skLineSegment(sketch, "E7.2.0.63", {"start": v(12, 6.27) * mm, "end": v(12, 4.27) * mm});
            skLineSegment(sketch, "E7.2.0.64", {"start": v(-12, -4.28) * mm, "end": v(-12, -6.28) * mm});
            skLineSegment(sketch, "E7.2.0.65", {"start": v(-68, 9.55) * mm, "end": v(-68, 4.27) * mm, "construction": true});
            skLineSegment(sketch, "E7.2.0.66", {"start": v(-42, -1) * mm, "end": v(-38, -1) * mm});
            skLineSegment(sketch, "E7.2.0.67", {"start": v(-52, 4.27) * mm, "end": v(-48, 4.27) * mm});
            skLineSegment(sketch, "E7.2.0.68", {"start": v(-72, -4.28) * mm, "end": v(-68, -4.28) * mm});
            skLineSegment(sketch, "E7.2.0.69", {"start": v(-12, -11.55) * mm, "end": v(-8, -11.55) * mm});
            skLineSegment(sketch, "E7.2.0.70", {"start": v(-18, 6.27) * mm, "end": v(-18, 4.27) * mm});
            skLineSegment(sketch, "E7.2.0.71", {"start": v(8, 6.27) * mm, "end": v(12, 6.27) * mm});
            skLineSegment(sketch, "E7.2.0.72", {"start": v(-2, -6.28) * mm, "end": v(2, -6.28) * mm});
            skLineSegment(sketch, "E7.2.0.73", {"start": v(-42, -11.55) * mm, "end": v(-38, -11.55) * mm});
            skLineSegment(sketch, "E7.2.0.74", {"start": v(-48, 6.27) * mm, "end": v(-48, 4.27) * mm});
            skLineSegment(sketch, "E7.2.0.75", {"start": v(-22, 6.27) * mm, "end": v(-18, 6.27) * mm});
            skLineSegment(sketch, "E7.2.0.76", {"start": v(-32, -6.28) * mm, "end": v(-28, -6.28) * mm});
            skLineSegment(sketch, "E7.2.0.77", {"start": v(-32, -9.55) * mm, "end": v(-32, -11.55) * mm});
            skLineSegment(sketch, "E7.2.0.78", {"start": v(-38, 1) * mm, "end": v(-38, -1) * mm});
            skLineSegment(sketch, "E7.2.0.79", {"start": v(-52, 6.27) * mm, "end": v(-48, 6.27) * mm});
            skLineSegment(sketch, "E7.2.0.80", {"start": v(-62, -6.28) * mm, "end": v(-58, -6.28) * mm});
            skLineSegment(sketch, "E7.2.0.81", {"start": v(-62, -9.55) * mm, "end": v(-62, -11.55) * mm});
            skLineSegment(sketch, "E7.2.0.82", {"start": v(-22, 6.27) * mm, "end": v(-22, 4.27) * mm});
            skLineSegment(sketch, "E7.2.0.83", {"start": v(12, 11.55) * mm, "end": v(12, 9.55) * mm});
            skLineSegment(sketch, "E7.2.0.84", {"start": v(2, -4.28) * mm, "end": v(2, -6.28) * mm});
            skLineSegment(sketch, "E7.2.0.85", {"start": v(-42, 1) * mm, "end": v(-38, 1) * mm});
            skLineSegment(sketch, "E7.2.0.86", {"start": v(-52, 6.27) * mm, "end": v(-52, 4.27) * mm});
            skLineSegment(sketch, "E7.2.0.87", {"start": v(-58, -9.55) * mm, "end": v(-58, -11.55) * mm});
            skLineSegment(sketch, "E7.2.0.88", {"start": v(-12, 1) * mm, "end": v(-12, -1) * mm});
            skLineSegment(sketch, "E7.2.0.89", {"start": v(-18, 11.55) * mm, "end": v(-18, 9.55) * mm});
            skLineSegment(sketch, "E7.2.0.90", {"start": v(-28, -4.28) * mm, "end": v(-28, -6.28) * mm});
            skLineSegment(sketch, "E7.2.0.91", {"start": v(8, 11.55) * mm, "end": v(8, 9.55) * mm});
            skLineSegment(sketch, "E7.2.0.92", {"start": v(-2, -4.28) * mm, "end": v(2, -4.28) * mm});
            skLineSegment(sketch, "E7.2.0.93", {"start": v(-42, 4.27) * mm, "end": v(-38, 4.27) * mm});
            skLineSegment(sketch, "E7.2.0.94", {"start": v(-52, 11.55) * mm, "end": v(-52, 9.55) * mm});
            skLineSegment(sketch, "E7.2.0.95", {"start": v(-62, -4.28) * mm, "end": v(-58, -4.28) * mm});
            skLineSegment(sketch, "E7.2.0.96", {"start": v(-22, 9.55) * mm, "end": v(-18, 9.55) * mm});
            skLineSegment(sketch, "E7.2.0.97", {"start": v(8, -6.28) * mm, "end": v(12, -6.28) * mm});
            skLineSegment(sketch, "E7.2.0.98", {"start": v(8, -9.55) * mm, "end": v(8, -11.55) * mm});
            skLineSegment(sketch, "E7.2.0.99", {"start": v(-48, 11.55) * mm, "end": v(-48, 9.55) * mm});
            skLineSegment(sketch, "E7.2.0.100", {"start": v(-62, -9.55) * mm, "end": v(-58, -9.55) * mm});
            skLineSegment(sketch, "E7.2.0.101", {"start": v(-12, 4.27) * mm, "end": v(-8, 4.27) * mm});
            skLineSegment(sketch, "E7.2.0.102", {"start": v(-22, 11.55) * mm, "end": v(-22, 9.55) * mm});
            skLineSegment(sketch, "E7.2.0.103", {"start": v(-32, -4.28) * mm, "end": v(-28, -4.28) * mm});
            skLineSegment(sketch, "E7.2.0.104", {"start": v(8, 9.55) * mm, "end": v(12, 9.55) * mm});
            skLineSegment(sketch, "E7.2.0.105", {"start": v(-2, -1) * mm, "end": v(2, -1) * mm});
            skLineSegment(sketch, "E7.2.0.106", {"start": v(-72, 4.27) * mm, "end": v(-68, 4.27) * mm});
            skLineSegment(sketch, "E7.2.0.107", {"start": v(-38, 6.27) * mm, "end": v(-38, 4.27) * mm});
            skLineSegment(sketch, "E7.2.0.108", {"start": v(-52, 9.55) * mm, "end": v(-48, 9.55) * mm});
            skLineSegment(sketch, "E7.2.0.109", {"start": v(-62, -4.28) * mm, "end": v(-62, -6.28) * mm});
            skLineSegment(sketch, "E7.2.0.110", {"start": v(2, 1) * mm, "end": v(2, -1) * mm});
            skLineSegment(sketch, "E7.2.0.111", {"start": v(-12, 6.27) * mm, "end": v(-8, 6.27) * mm});
            skLineSegment(sketch, "E7.2.0.112", {"start": v(-22, -6.28) * mm, "end": v(-18, -6.28) * mm});
            skLineSegment(sketch, "E7.2.0.113", {"start": v(8, 11.55) * mm, "end": v(12, 11.55) * mm});
            skLineSegment(sketch, "E7.2.0.114", {"start": v(-62, -11.55) * mm, "end": v(-58, -11.55) * mm});
            skLineSegment(sketch, "E7.2.0.115", {"start": v(-68, 6.27) * mm, "end": v(-68, 4.27) * mm});
            skLineSegment(sketch, "E7.2.0.116", {"start": v(-42, 6.27) * mm, "end": v(-38, 6.27) * mm});
            skLineSegment(sketch, "E7.2.0.117", {"start": v(-52, -6.28) * mm, "end": v(-48, -6.28) * mm});
            skLineSegment(sketch, "E7.2.0.118", {"start": v(-2, 1) * mm, "end": v(2, 1) * mm});
            skLineSegment(sketch, "E7.2.0.119", {"start": v(-12, 6.27) * mm, "end": v(-12, 4.27) * mm});
            skLineSegment(sketch, "E7.2.0.120", {"start": v(-22, 11.55) * mm, "end": v(-18, 11.55) * mm});
            skLineSegment(sketch, "E7.2.0.121", {"start": v(12, -4.28) * mm, "end": v(12, -6.28) * mm});
            skLineSegment(sketch, "E7.2.0.122", {"start": v(-58, 1) * mm, "end": v(-58, -1) * mm});
            skLineSegment(sketch, "E7.2.0.123", {"start": v(-72, 6.27) * mm, "end": v(-68, 6.27) * mm});
            skLineSegment(sketch, "E7.2.0.124", {"start": v(-82, -6.28) * mm, "end": v(-78, -6.28) * mm});
            skLineSegment(sketch, "E7.2.0.125", {"start": v(-42, 6.27) * mm, "end": v(-42, 4.27) * mm});
            skLineSegment(sketch, "E7.2.0.126", {"start": v(-52, 11.55) * mm, "end": v(-48, 11.55) * mm});
            skLineSegment(sketch, "E7.2.0.127", {"start": v(-2, 1) * mm, "end": v(-2, -1) * mm});
            skLineSegment(sketch, "E7.2.0.128", {"start": v(-8, 11.55) * mm, "end": v(-8, 9.55) * mm});
            skLineSegment(sketch, "E7.2.0.129", {"start": v(-18, -4.28) * mm, "end": v(-18, -6.28) * mm});
            skLineSegment(sketch, "E7.2.0.130", {"start": v(8, -4.28) * mm, "end": v(12, -4.28) * mm});
            skLineSegment(sketch, "E7.2.0.131", {"start": v(12, 9.55) * mm, "end": v(12, 4.27) * mm, "construction": true});
            skLineSegment(sketch, "E7.2.0.132", {"start": v(-32, 1) * mm, "end": v(-32, -1) * mm});
            skLineSegment(sketch, "E7.2.0.133", {"start": v(-38, 11.55) * mm, "end": v(-38, 9.55) * mm});
            skLineSegment(sketch, "E7.2.0.134", {"start": v(-48, -4.28) * mm, "end": v(-48, -6.28) * mm});
            skLineSegment(sketch, "E7.2.0.135", {"start": v(-22, -4.28) * mm, "end": v(-18, -4.28) * mm});
            skLineSegment(sketch, "E7.2.0.136", {"start": v(-18, 9.55) * mm, "end": v(-18, 4.27) * mm, "construction": true});
            skLineSegment(sketch, "E7.2.0.137", {"start": v(8, -4.28) * mm, "end": v(8, -6.28) * mm});
            skLineSegment(sketch, "E7.2.0.138", {"start": v(-62, 1) * mm, "end": v(-58, 1) * mm});
            skLineSegment(sketch, "E7.2.0.139", {"start": v(-82, -9.55) * mm, "end": v(-82, -11.55) * mm});
            skLineSegment(sketch, "E7.2.0.140", {"start": v(-22, -4.28) * mm, "end": v(-22, -6.28) * mm});
            skLineSegment(sketch, "E7.2.0.141", {"start": v(-82, -11.55) * mm, "end": v(-72, -11.55) * mm, "construction": true});
            skLineSegment(sketch, "E7.2.0.142", {"start": v(-68, 11.55) * mm, "end": v(-68, 9.55) * mm});
            skLineSegment(sketch, "E7.2.0.143", {"start": v(-82, -9.55) * mm, "end": v(-78, -9.55) * mm});
            skLineSegment(sketch, "E7.2.0.144", {"start": v(-42, 11.55) * mm, "end": v(-42, 9.55) * mm});
            skLineSegment(sketch, "E7.2.0.145", {"start": v(-52, -4.28) * mm, "end": v(-48, -4.28) * mm});
            skLineSegment(sketch, "E7.2.0.146", {"start": v(-48, 9.55) * mm, "end": v(-48, 4.27) * mm, "construction": true});
            skLineSegment(sketch, "E7.2.0.147", {"start": v(-62, 4.27) * mm, "end": v(-58, 4.27) * mm});
            skLineSegment(sketch, "E7.2.0.148", {"start": v(-72, 11.55) * mm, "end": v(-72, 9.55) * mm});
            skLineSegment(sketch, "E7.2.0.149", {"start": v(-78, -9.55) * mm, "end": v(-78, -11.55) * mm});
            skLineSegment(sketch, "E7.2.0.150", {"start": v(-42, 9.55) * mm, "end": v(-38, 9.55) * mm});
            skLineSegment(sketch, "E7.2.0.151", {"start": v(-52, -4.28) * mm, "end": v(-52, -6.28) * mm});
            skLineSegment(sketch, "E7.2.0.152", {"start": v(-52, -1) * mm, "end": v(-48, -1) * mm});
            skLineSegment(sketch, "E7.2.0.153", {"start": v(-12, -6.28) * mm, "end": v(-8, -6.28) * mm});
            skLineSegment(sketch, "E7.2.0.154", {"start": v(-12, -9.55) * mm, "end": v(-12, -11.55) * mm});
            skLineSegment(sketch, "E7.2.0.155", {"start": v(-82, -4.28) * mm, "end": v(-82, -6.28) * mm});
            skLineSegment(sketch, "E7.2.0.156", {"start": v(-82, -4.28) * mm, "end": v(-78, -4.28) * mm});
            skLineSegment(sketch, "E7.2.0.157", {"start": v(-78, -4.28) * mm, "end": v(-78, -6.28) * mm});
            skLineSegment(sketch, "E7.2.0.158", {"start": v(-78, 6.27) * mm, "end": v(-78, 4.27) * mm});
            skLineSegment(sketch, "E7.2.0.159", {"start": v(-82, 1) * mm, "end": v(-82, -1) * mm});
            skLineSegment(sketch, "E7.2.0.160", {"start": v(-82, 1) * mm, "end": v(-78, 1) * mm});
            skLineSegment(sketch, "E7.2.0.161", {"start": v(-72, 9.55) * mm, "end": v(-68, 9.55) * mm});
            skLineSegment(sketch, "E7.2.0.162", {"start": v(-82, -11.55) * mm, "end": v(-78, -11.55) * mm});
            skLineSegment(sketch, "E7.2.0.163", {"start": v(-82, -1) * mm, "end": v(-78, -1) * mm});
            skLineSegment(sketch, "E7.2.0.164", {"start": v(-42, -6.28) * mm, "end": v(-38, -6.28) * mm});
            skLineSegment(sketch, "E7.2.0.165", {"start": v(-42, -9.55) * mm, "end": v(-42, -11.55) * mm});
            skLineSegment(sketch, "E7.2.0.166", {"start": v(-8, -9.55) * mm, "end": v(-8, -11.55) * mm});
            skLineSegment(sketch, "E7.2.0.167", {"start": v(-62, 6.27) * mm, "end": v(-58, 6.27) * mm});
            skLineSegment(sketch, "E7.2.0.168", {"start": v(-72, -6.28) * mm, "end": v(-68, -6.28) * mm});
            skLineSegment(sketch, "E7.2.0.169", {"start": v(-72, -9.55) * mm, "end": v(-72, -11.55) * mm});
            skLineSegment(sketch, "E7.2.0.170", {"start": v(-42, 11.55) * mm, "end": v(-38, 11.55) * mm});
            skLineSegment(sketch, "E7.2.0.171", {"start": v(-38, -9.55) * mm, "end": v(-38, -11.55) * mm});
            skLineSegment(sketch, "E7.2.0.172", {"start": v(-48, 1) * mm, "end": v(-48, -1) * mm});
            skLineSegment(sketch, "E7.2.0.173", {"start": v(-12, -9.55) * mm, "end": v(-8, -9.55) * mm});
            skLineSegment(sketch, "E7.2.0.174", {"start": v(-8, 9.55) * mm, "end": v(-8, 4.27) * mm, "construction": true});
            skLineSegment(sketch, "E7.2.0.175", {"start": v(-22, 1) * mm, "end": v(-22, -1) * mm});
            skLineSegment(sketch, "E7.2.0.176", {"start": v(-42, -4.28) * mm, "end": v(-42, -6.28) * mm});
            skLineSegment(sketch, "E7.2.0.177", {"start": v(-72, -1) * mm, "end": v(-68, -1) * mm});
            skLineSegment(sketch, "E7.2.0.178", {"start": v(-72, -4.28) * mm, "end": v(-72, -6.28) * mm});
            skLineSegment(sketch, "E7.2.0.179", {"start": v(-68, 1) * mm, "end": v(-68, -1) * mm});
            skLineSegment(sketch, "E7.2.0.180", {"start": v(2, 9.55) * mm, "end": v(2, 4.27) * mm, "construction": true});
            skLineSegment(sketch, "E7.2.0.181", {"start": v(-58, 9.55) * mm, "end": v(-58, 4.27) * mm, "construction": true});
            skLineSegment(sketch, "E7.2.0.182", {"start": v(-72, 1) * mm, "end": v(-72, -1) * mm});
            skLineSegment(sketch, "E7.2.0.183", {"start": v(-8, 6.27) * mm, "end": v(-8, 4.27) * mm});
            skLineSegment(sketch, "E7.2.0.184", {"start": v(-32, -4.28) * mm, "end": v(-32, -6.28) * mm});
            skLineSegment(sketch, "E7.2.0.185", {"start": v(-72, 1) * mm, "end": v(-68, 1) * mm});
            skLineSegment(sketch, "E7.2.0.186", {"start": v(-42, 1) * mm, "end": v(-42, -1) * mm});
            skLineSegment(sketch, "E7.2.0.187", {"start": v(-58, -4.28) * mm, "end": v(-58, -6.28) * mm});
            skLineSegment(sketch, "E7.2.0.188", {"start": v(-28, 9.55) * mm, "end": v(-28, 4.27) * mm, "construction": true});
            skLineSegment(sketch, "E7.2.0.189", {"start": v(-2, -4.28) * mm, "end": v(-2, -6.28) * mm});
            skLineSegment(sketch, "E7.2.0.190", {"start": v(-2, 4.27) * mm, "end": v(2, 4.27) * mm});
            skLineSegment(sketch, "E7.2.0.191", {"start": v(8, -1) * mm, "end": v(12, -1) * mm});
            skLineSegment(sketch, "E7.2.0.192", {"start": v(2, 6.27) * mm, "end": v(2, 4.27) * mm});
            skLineSegment(sketch, "E7.2.0.193", {"start": v(-22, -1) * mm, "end": v(-18, -1) * mm});
            skLineSegment(sketch, "E7.2.0.194", {"start": v(-32, 4.27) * mm, "end": v(-28, 4.27) * mm});
            skLineSegment(sketch, "E7.2.0.195", {"start": v(12, 1) * mm, "end": v(12, -1) * mm});
            skLineSegment(sketch, "E7.2.0.196", {"start": v(-28, 6.27) * mm, "end": v(-28, 4.27) * mm});
            skLineSegment(sketch, "E7.2.0.197", {"start": v(-2, 6.27) * mm, "end": v(2, 6.27) * mm});
            skLineSegment(sketch, "E7.2.0.198", {"start": v(-78, 11.55) * mm, "end": v(-78, 9.55) * mm});
            skLineSegment(sketch, "E7.2.0.199", {"start": v(-78, 1) * mm, "end": v(-78, -1) * mm});
            skLineSegment(sketch, "E7.2.0.200", {"start": v(-58, 6.27) * mm, "end": v(-58, 4.27) * mm});
            skLineSegment(sketch, "E7.2.0.201", {"start": v(-32, 6.27) * mm, "end": v(-28, 6.27) * mm});
            skLineSegment(sketch, "E7.2.0.202", {"start": v(-78, 9.55) * mm, "end": v(-78, 4.27) * mm, "construction": true});
            skLineSegment(sketch, "E7.2.0.203", {"start": v(-2, 6.27) * mm, "end": v(-2, 4.27) * mm});
            skLineSegment(sketch, "E7.2.0.204", {"start": v(-18, 1) * mm, "end": v(-18, -1) * mm});
            skLineSegment(sketch, "E7.2.0.205", {"start": v(8, 1) * mm, "end": v(12, 1) * mm});
            skLineSegment(sketch, "E7.2.0.206", {"start": v(-32, 6.27) * mm, "end": v(-32, 4.27) * mm});
            skLineSegment(sketch, "E7.2.0.207", {"start": v(2, 11.55) * mm, "end": v(2, 9.55) * mm});
            skLineSegment(sketch, "E7.2.0.208", {"start": v(-8, -4.28) * mm, "end": v(-8, -6.28) * mm});
            skLineSegment(sketch, "E7.2.0.209", {"start": v(-22, 1) * mm, "end": v(-18, 1) * mm});
            skLineSegment(sketch, "E7.2.0.210", {"start": v(8, 1) * mm, "end": v(8, -1) * mm});
            skLineSegment(sketch, "E7.3.0.0", {"start": v(28, -9.55) * mm, "end": v(32, -9.55) * mm});
            skLineSegment(sketch, "E7.3.0.1", {"start": v(32, -9.55) * mm, "end": v(32, -11.55) * mm});
            skLineSegment(sketch, "E7.3.0.2", {"start": v(98, 11.55) * mm, "end": v(98, 9.55) * mm});
            skLineSegment(sketch, "E7.3.0.3", {"start": v(88, -1) * mm, "end": v(92, -1) * mm});
            skLineSegment(sketch, "E7.3.0.4", {"start": v(68, 11.55) * mm, "end": v(68, 9.55) * mm});
            skLineSegment(sketch, "E7.3.0.5", {"start": v(98, 9.55) * mm, "end": v(102, 9.55) * mm});
            skLineSegment(sketch, "E7.3.0.6", {"start": v(38, 11.55) * mm, "end": v(38, 9.55) * mm});
            skLineSegment(sketch, "E7.3.0.7", {"start": v(68, 9.55) * mm, "end": v(72, 9.55) * mm});
            skLineSegment(sketch, "E7.3.0.8", {"start": v(98, -9.55) * mm, "end": v(98, -11.55) * mm});
            skLineSegment(sketch, "E7.3.0.9", {"start": v(38, 9.55) * mm, "end": v(42, 9.55) * mm});
            skLineSegment(sketch, "E7.3.0.10", {"start": v(92, 1) * mm, "end": v(92, -1) * mm});
            skLineSegment(sketch, "E7.3.0.11", {"start": v(108, 6.27) * mm, "end": v(108, 4.27) * mm});
            skLineSegment(sketch, "E7.3.0.12", {"start": v(98, 11.55) * mm, "end": v(102, 11.55) * mm});
            skLineSegment(sketch, "E7.3.0.13", {"start": v(102, -9.55) * mm, "end": v(102, -11.55) * mm});
            skLineSegment(sketch, "E7.3.0.14", {"start": v(28, -11.55) * mm, "end": v(32, -11.55) * mm});
            skLineSegment(sketch, "E7.3.0.15", {"start": v(88, 1) * mm, "end": v(92, 1) * mm});
            skLineSegment(sketch, "E7.3.0.16", {"start": v(68, 11.55) * mm, "end": v(72, 11.55) * mm});
            skLineSegment(sketch, "E7.3.0.17", {"start": v(72, -9.55) * mm, "end": v(72, -11.55) * mm});
            skLineSegment(sketch, "E7.3.0.18", {"start": v(98, -9.55) * mm, "end": v(102, -9.55) * mm});
            skLineSegment(sketch, "E7.3.0.19", {"start": v(38, 11.55) * mm, "end": v(42, 11.55) * mm});
            skLineSegment(sketch, "E7.3.0.20", {"start": v(68, -9.55) * mm, "end": v(72, -9.55) * mm});
            skLineSegment(sketch, "E7.3.0.21", {"start": v(68, -1) * mm, "end": v(72, -1) * mm});
            skLineSegment(sketch, "E7.3.0.22", {"start": v(98, -11.55) * mm, "end": v(102, -11.55) * mm});
            skLineSegment(sketch, "E7.3.0.23", {"start": v(38, -1) * mm, "end": v(42, -1) * mm});
            skLineSegment(sketch, "E7.3.0.24", {"start": v(68, -11.55) * mm, "end": v(72, -11.55) * mm});
            skLineSegment(sketch, "E7.3.0.25", {"start": v(78, -9.55) * mm, "end": v(78, -11.55) * mm});
            skLineSegment(sketch, "E7.3.0.26", {"start": v(112, -9.55) * mm, "end": v(112, -11.55) * mm});
            skLineSegment(sketch, "E7.3.0.27", {"start": v(72, 1) * mm, "end": v(72, -1) * mm});
            skLineSegment(sketch, "E7.3.0.28", {"start": v(48, -9.55) * mm, "end": v(48, -11.55) * mm});
            skLineSegment(sketch, "E7.3.0.29", {"start": v(82, -9.55) * mm, "end": v(82, -11.55) * mm});
            skLineSegment(sketch, "E7.3.0.30", {"start": v(108, -9.55) * mm, "end": v(112, -9.55) * mm});
            skLineSegment(sketch, "E7.3.0.31", {"start": v(68, 1) * mm, "end": v(72, 1) * mm});
            skLineSegment(sketch, "E7.3.0.32", {"start": v(52, -9.55) * mm, "end": v(52, -11.55) * mm});
            skLineSegment(sketch, "E7.3.0.33", {"start": v(78, -9.55) * mm, "end": v(82, -9.55) * mm});
            skLineSegment(sketch, "E7.3.0.34", {"start": v(48, -9.55) * mm, "end": v(52, -9.55) * mm});
            skLineSegment(sketch, "E7.3.0.35", {"start": v(88, 11.55) * mm, "end": v(88, 9.55) * mm});
            skLineSegment(sketch, "E7.3.0.36", {"start": v(28, 6.27) * mm, "end": v(28, 4.27) * mm});
            skLineSegment(sketch, "E7.3.0.37", {"start": v(88, 9.55) * mm, "end": v(92, 9.55) * mm});
            skLineSegment(sketch, "E7.3.0.38", {"start": v(108, -11.55) * mm, "end": v(112, -11.55) * mm});
            skLineSegment(sketch, "E7.3.0.39", {"start": v(38, 1) * mm, "end": v(38, -1) * mm});
            skLineSegment(sketch, "E7.3.0.40", {"start": v(78, -11.55) * mm, "end": v(82, -11.55) * mm});
            skLineSegment(sketch, "E7.3.0.41", {"start": v(18, 11.55) * mm, "end": v(22, 11.55) * mm});
            skLineSegment(sketch, "E7.3.0.42", {"start": v(18, 9.55) * mm, "end": v(22, 9.55) * mm});
            skLineSegment(sketch, "E7.3.0.43", {"start": v(18, 11.55) * mm, "end": v(18, 9.55) * mm});
            skLineSegment(sketch, "E7.3.0.44", {"start": v(18, 6.27) * mm, "end": v(18, 4.27) * mm});
            skLineSegment(sketch, "E7.3.0.45", {"start": v(18, 6.27) * mm, "end": v(22, 6.27) * mm});
            skLineSegment(sketch, "E7.3.0.46", {"start": v(18, 4.27) * mm, "end": v(22, 4.27) * mm});
            skLineSegment(sketch, "E7.3.0.47", {"start": v(48, -11.55) * mm, "end": v(52, -11.55) * mm});
            skLineSegment(sketch, "E7.3.0.48", {"start": v(88, 11.55) * mm, "end": v(92, 11.55) * mm});
            skLineSegment(sketch, "E7.3.0.49", {"start": v(38, 6.27) * mm, "end": v(38, 4.27) * mm});
            skLineSegment(sketch, "E7.3.0.50", {"start": v(28, 11.55) * mm, "end": v(32, 11.55) * mm});
            skLineSegment(sketch, "E7.3.0.51", {"start": v(72, 11.55) * mm, "end": v(72, 9.55) * mm});
            skLineSegment(sketch, "E7.3.0.52", {"start": v(62, -4.28) * mm, "end": v(62, -6.28) * mm});
            skLineSegment(sketch, "E7.3.0.53", {"start": v(58, -9.55) * mm, "end": v(62, -9.55) * mm});
            skLineSegment(sketch, "E7.3.0.54", {"start": v(48, 1) * mm, "end": v(52, 1) * mm});
            skLineSegment(sketch, "E7.3.0.55", {"start": v(88, -4.28) * mm, "end": v(92, -4.28) * mm});
            skLineSegment(sketch, "E7.3.0.56", {"start": v(108, 4.27) * mm, "end": v(112, 4.27) * mm});
            skLineSegment(sketch, "E7.3.0.57", {"start": v(62, 9.55) * mm, "end": v(62, 4.27) * mm, "construction": true});
            skLineSegment(sketch, "E7.3.0.58", {"start": v(48, 1) * mm, "end": v(48, -1) * mm});
            skLineSegment(sketch, "E7.3.0.59", {"start": v(42, 11.55) * mm, "end": v(42, 9.55) * mm});
            skLineSegment(sketch, "E7.3.0.60", {"start": v(32, -4.28) * mm, "end": v(32, -6.28) * mm});
            skLineSegment(sketch, "E7.3.0.61", {"start": v(78, 4.27) * mm, "end": v(82, 4.27) * mm});
            skLineSegment(sketch, "E7.3.0.62", {"start": v(58, -4.28) * mm, "end": v(62, -4.28) * mm});
            skLineSegment(sketch, "E7.3.0.63", {"start": v(112, 6.27) * mm, "end": v(112, 4.27) * mm});
            skLineSegment(sketch, "E7.3.0.64", {"start": v(88, -4.28) * mm, "end": v(88, -6.28) * mm});
            skLineSegment(sketch, "E7.3.0.65", {"start": v(32, 9.55) * mm, "end": v(32, 4.27) * mm, "construction": true});
            skLineSegment(sketch, "E7.3.0.66", {"start": v(58, -1) * mm, "end": v(62, -1) * mm});
            skLineSegment(sketch, "E7.3.0.67", {"start": v(48, 4.27) * mm, "end": v(52, 4.27) * mm});
            skLineSegment(sketch, "E7.3.0.68", {"start": v(28, -4.28) * mm, "end": v(32, -4.28) * mm});
            skLineSegment(sketch, "E7.3.0.69", {"start": v(88, -11.55) * mm, "end": v(92, -11.55) * mm});
            skLineSegment(sketch, "E7.3.0.70", {"start": v(82, 6.27) * mm, "end": v(82, 4.27) * mm});
            skLineSegment(sketch, "E7.3.0.71", {"start": v(108, 6.27) * mm, "end": v(112, 6.27) * mm});
            skLineSegment(sketch, "E7.3.0.72", {"start": v(98, -6.28) * mm, "end": v(102, -6.28) * mm});
            skLineSegment(sketch, "E7.3.0.73", {"start": v(58, -11.55) * mm, "end": v(62, -11.55) * mm});
            skLineSegment(sketch, "E7.3.0.74", {"start": v(52, 6.27) * mm, "end": v(52, 4.27) * mm});
            skLineSegment(sketch, "E7.3.0.75", {"start": v(78, 6.27) * mm, "end": v(82, 6.27) * mm});
            skLineSegment(sketch, "E7.3.0.76", {"start": v(68, -6.28) * mm, "end": v(72, -6.28) * mm});
            skLineSegment(sketch, "E7.3.0.77", {"start": v(68, -9.55) * mm, "end": v(68, -11.55) * mm});
            skLineSegment(sketch, "E7.3.0.78", {"start": v(62, 1) * mm, "end": v(62, -1) * mm});
            skLineSegment(sketch, "E7.3.0.79", {"start": v(48, 6.27) * mm, "end": v(52, 6.27) * mm});
            skLineSegment(sketch, "E7.3.0.80", {"start": v(38, -6.28) * mm, "end": v(42, -6.28) * mm});
            skLineSegment(sketch, "E7.3.0.81", {"start": v(38, -9.55) * mm, "end": v(38, -11.55) * mm});
            skLineSegment(sketch, "E7.3.0.82", {"start": v(78, 6.27) * mm, "end": v(78, 4.27) * mm});
            skLineSegment(sketch, "E7.3.0.83", {"start": v(112, 11.55) * mm, "end": v(112, 9.55) * mm});
            skLineSegment(sketch, "E7.3.0.84", {"start": v(102, -4.28) * mm, "end": v(102, -6.28) * mm});
            skLineSegment(sketch, "E7.3.0.85", {"start": v(58, 1) * mm, "end": v(62, 1) * mm});
            skLineSegment(sketch, "E7.3.0.86", {"start": v(48, 6.27) * mm, "end": v(48, 4.27) * mm});
            skLineSegment(sketch, "E7.3.0.87", {"start": v(42, -9.55) * mm, "end": v(42, -11.55) * mm});
            skLineSegment(sketch, "E7.3.0.88", {"start": v(88, 1) * mm, "end": v(88, -1) * mm});
            skLineSegment(sketch, "E7.3.0.89", {"start": v(82, 11.55) * mm, "end": v(82, 9.55) * mm});
            skLineSegment(sketch, "E7.3.0.90", {"start": v(72, -4.28) * mm, "end": v(72, -6.28) * mm});
            skLineSegment(sketch, "E7.3.0.91", {"start": v(108, 11.55) * mm, "end": v(108, 9.55) * mm});
            skLineSegment(sketch, "E7.3.0.92", {"start": v(98, -4.28) * mm, "end": v(102, -4.28) * mm});
            skLineSegment(sketch, "E7.3.0.93", {"start": v(58, 4.27) * mm, "end": v(62, 4.27) * mm});
            skLineSegment(sketch, "E7.3.0.94", {"start": v(48, 11.55) * mm, "end": v(48, 9.55) * mm});
            skLineSegment(sketch, "E7.3.0.95", {"start": v(38, -4.28) * mm, "end": v(42, -4.28) * mm});
            skLineSegment(sketch, "E7.3.0.96", {"start": v(78, 9.55) * mm, "end": v(82, 9.55) * mm});
            skLineSegment(sketch, "E7.3.0.97", {"start": v(108, -6.28) * mm, "end": v(112, -6.28) * mm});
            skLineSegment(sketch, "E7.3.0.98", {"start": v(108, -9.55) * mm, "end": v(108, -11.55) * mm});
            skLineSegment(sketch, "E7.3.0.99", {"start": v(52, 11.55) * mm, "end": v(52, 9.55) * mm});
            skLineSegment(sketch, "E7.3.0.100", {"start": v(38, -9.55) * mm, "end": v(42, -9.55) * mm});
            skLineSegment(sketch, "E7.3.0.101", {"start": v(88, 4.27) * mm, "end": v(92, 4.27) * mm});
            skLineSegment(sketch, "E7.3.0.102", {"start": v(78, 11.55) * mm, "end": v(78, 9.55) * mm});
            skLineSegment(sketch, "E7.3.0.103", {"start": v(68, -4.28) * mm, "end": v(72, -4.28) * mm});
            skLineSegment(sketch, "E7.3.0.104", {"start": v(108, 9.55) * mm, "end": v(112, 9.55) * mm});
            skLineSegment(sketch, "E7.3.0.105", {"start": v(98, -1) * mm, "end": v(102, -1) * mm});
            skLineSegment(sketch, "E7.3.0.106", {"start": v(28, 4.27) * mm, "end": v(32, 4.27) * mm});
            skLineSegment(sketch, "E7.3.0.107", {"start": v(62, 6.27) * mm, "end": v(62, 4.27) * mm});
            skLineSegment(sketch, "E7.3.0.108", {"start": v(48, 9.55) * mm, "end": v(52, 9.55) * mm});
            skLineSegment(sketch, "E7.3.0.109", {"start": v(38, -4.28) * mm, "end": v(38, -6.28) * mm});
            skLineSegment(sketch, "E7.3.0.110", {"start": v(102, 1) * mm, "end": v(102, -1) * mm});
            skLineSegment(sketch, "E7.3.0.111", {"start": v(88, 6.27) * mm, "end": v(92, 6.27) * mm});
            skLineSegment(sketch, "E7.3.0.112", {"start": v(78, -6.28) * mm, "end": v(82, -6.28) * mm});
            skLineSegment(sketch, "E7.3.0.113", {"start": v(108, 11.55) * mm, "end": v(112, 11.55) * mm});
            skLineSegment(sketch, "E7.3.0.114", {"start": v(38, -11.55) * mm, "end": v(42, -11.55) * mm});
            skLineSegment(sketch, "E7.3.0.115", {"start": v(32, 6.27) * mm, "end": v(32, 4.27) * mm});
            skLineSegment(sketch, "E7.3.0.116", {"start": v(58, 6.27) * mm, "end": v(62, 6.27) * mm});
            skLineSegment(sketch, "E7.3.0.117", {"start": v(48, -6.28) * mm, "end": v(52, -6.28) * mm});
            skLineSegment(sketch, "E7.3.0.118", {"start": v(98, 1) * mm, "end": v(102, 1) * mm});
            skLineSegment(sketch, "E7.3.0.119", {"start": v(88, 6.27) * mm, "end": v(88, 4.27) * mm});
            skLineSegment(sketch, "E7.3.0.120", {"start": v(78, 11.55) * mm, "end": v(82, 11.55) * mm});
            skLineSegment(sketch, "E7.3.0.121", {"start": v(112, -4.28) * mm, "end": v(112, -6.28) * mm});
            skLineSegment(sketch, "E7.3.0.122", {"start": v(42, 1) * mm, "end": v(42, -1) * mm});
            skLineSegment(sketch, "E7.3.0.123", {"start": v(28, 6.27) * mm, "end": v(32, 6.27) * mm});
            skLineSegment(sketch, "E7.3.0.124", {"start": v(18, -6.28) * mm, "end": v(22, -6.28) * mm});
            skLineSegment(sketch, "E7.3.0.125", {"start": v(58, 6.27) * mm, "end": v(58, 4.27) * mm});
            skLineSegment(sketch, "E7.3.0.126", {"start": v(48, 11.55) * mm, "end": v(52, 11.55) * mm});
            skLineSegment(sketch, "E7.3.0.127", {"start": v(98, 1) * mm, "end": v(98, -1) * mm});
            skLineSegment(sketch, "E7.3.0.128", {"start": v(92, 11.55) * mm, "end": v(92, 9.55) * mm});
            skLineSegment(sketch, "E7.3.0.129", {"start": v(82, -4.28) * mm, "end": v(82, -6.28) * mm});
            skLineSegment(sketch, "E7.3.0.130", {"start": v(108, -4.28) * mm, "end": v(112, -4.28) * mm});
            skLineSegment(sketch, "E7.3.0.131", {"start": v(112, 9.55) * mm, "end": v(112, 4.27) * mm, "construction": true});
            skLineSegment(sketch, "E7.3.0.132", {"start": v(68, 1) * mm, "end": v(68, -1) * mm});
            skLineSegment(sketch, "E7.3.0.133", {"start": v(62, 11.55) * mm, "end": v(62, 9.55) * mm});
            skLineSegment(sketch, "E7.3.0.134", {"start": v(52, -4.28) * mm, "end": v(52, -6.28) * mm});
            skLineSegment(sketch, "E7.3.0.135", {"start": v(78, -4.28) * mm, "end": v(82, -4.28) * mm});
            skLineSegment(sketch, "E7.3.0.136", {"start": v(82, 9.55) * mm, "end": v(82, 4.27) * mm, "construction": true});
            skLineSegment(sketch, "E7.3.0.137", {"start": v(108, -4.28) * mm, "end": v(108, -6.28) * mm});
            skLineSegment(sketch, "E7.3.0.138", {"start": v(38, 1) * mm, "end": v(42, 1) * mm});
            skLineSegment(sketch, "E7.3.0.139", {"start": v(18, -9.55) * mm, "end": v(18, -11.55) * mm});
            skLineSegment(sketch, "E7.3.0.140", {"start": v(78, -4.28) * mm, "end": v(78, -6.28) * mm});
            skLineSegment(sketch, "E7.3.0.141", {"start": v(18, -11.55) * mm, "end": v(28, -11.55) * mm, "construction": true});
            skLineSegment(sketch, "E7.3.0.142", {"start": v(32, 11.55) * mm, "end": v(32, 9.55) * mm});
            skLineSegment(sketch, "E7.3.0.143", {"start": v(18, -9.55) * mm, "end": v(22, -9.55) * mm});
            skLineSegment(sketch, "E7.3.0.144", {"start": v(58, 11.55) * mm, "end": v(58, 9.55) * mm});
            skLineSegment(sketch, "E7.3.0.145", {"start": v(48, -4.28) * mm, "end": v(52, -4.28) * mm});
            skLineSegment(sketch, "E7.3.0.146", {"start": v(52, 9.55) * mm, "end": v(52, 4.27) * mm, "construction": true});
            skLineSegment(sketch, "E7.3.0.147", {"start": v(38, 4.27) * mm, "end": v(42, 4.27) * mm});
            skLineSegment(sketch, "E7.3.0.148", {"start": v(28, 11.55) * mm, "end": v(28, 9.55) * mm});
            skLineSegment(sketch, "E7.3.0.149", {"start": v(22, -9.55) * mm, "end": v(22, -11.55) * mm});
            skLineSegment(sketch, "E7.3.0.150", {"start": v(58, 9.55) * mm, "end": v(62, 9.55) * mm});
            skLineSegment(sketch, "E7.3.0.151", {"start": v(48, -4.28) * mm, "end": v(48, -6.28) * mm});
            skLineSegment(sketch, "E7.3.0.152", {"start": v(48, -1) * mm, "end": v(52, -1) * mm});
            skLineSegment(sketch, "E7.3.0.153", {"start": v(88, -6.28) * mm, "end": v(92, -6.28) * mm});
            skLineSegment(sketch, "E7.3.0.154", {"start": v(88, -9.55) * mm, "end": v(88, -11.55) * mm});
            skLineSegment(sketch, "E7.3.0.155", {"start": v(18, -4.28) * mm, "end": v(18, -6.28) * mm});
            skLineSegment(sketch, "E7.3.0.156", {"start": v(18, -4.28) * mm, "end": v(22, -4.28) * mm});
            skLineSegment(sketch, "E7.3.0.157", {"start": v(22, -4.28) * mm, "end": v(22, -6.28) * mm});
            skLineSegment(sketch, "E7.3.0.158", {"start": v(22, 6.27) * mm, "end": v(22, 4.27) * mm});
            skLineSegment(sketch, "E7.3.0.159", {"start": v(18, 1) * mm, "end": v(18, -1) * mm});
            skLineSegment(sketch, "E7.3.0.160", {"start": v(18, 1) * mm, "end": v(22, 1) * mm});
            skLineSegment(sketch, "E7.3.0.161", {"start": v(28, 9.55) * mm, "end": v(32, 9.55) * mm});
            skLineSegment(sketch, "E7.3.0.162", {"start": v(18, -11.55) * mm, "end": v(22, -11.55) * mm});
            skLineSegment(sketch, "E7.3.0.163", {"start": v(18, -1) * mm, "end": v(22, -1) * mm});
            skLineSegment(sketch, "E7.3.0.164", {"start": v(58, -6.28) * mm, "end": v(62, -6.28) * mm});
            skLineSegment(sketch, "E7.3.0.165", {"start": v(58, -9.55) * mm, "end": v(58, -11.55) * mm});
            skLineSegment(sketch, "E7.3.0.166", {"start": v(92, -9.55) * mm, "end": v(92, -11.55) * mm});
            skLineSegment(sketch, "E7.3.0.167", {"start": v(38, 6.27) * mm, "end": v(42, 6.27) * mm});
            skLineSegment(sketch, "E7.3.0.168", {"start": v(28, -6.28) * mm, "end": v(32, -6.28) * mm});
            skLineSegment(sketch, "E7.3.0.169", {"start": v(28, -9.55) * mm, "end": v(28, -11.55) * mm});
            skLineSegment(sketch, "E7.3.0.170", {"start": v(58, 11.55) * mm, "end": v(62, 11.55) * mm});
            skLineSegment(sketch, "E7.3.0.171", {"start": v(62, -9.55) * mm, "end": v(62, -11.55) * mm});
            skLineSegment(sketch, "E7.3.0.172", {"start": v(52, 1) * mm, "end": v(52, -1) * mm});
            skLineSegment(sketch, "E7.3.0.173", {"start": v(88, -9.55) * mm, "end": v(92, -9.55) * mm});
            skLineSegment(sketch, "E7.3.0.174", {"start": v(92, 9.55) * mm, "end": v(92, 4.27) * mm, "construction": true});
            skLineSegment(sketch, "E7.3.0.175", {"start": v(78, 1) * mm, "end": v(78, -1) * mm});
            skLineSegment(sketch, "E7.3.0.176", {"start": v(58, -4.28) * mm, "end": v(58, -6.28) * mm});
            skLineSegment(sketch, "E7.3.0.177", {"start": v(28, -1) * mm, "end": v(32, -1) * mm});
            skLineSegment(sketch, "E7.3.0.178", {"start": v(28, -4.28) * mm, "end": v(28, -6.28) * mm});
            skLineSegment(sketch, "E7.3.0.179", {"start": v(32, 1) * mm, "end": v(32, -1) * mm});
            skLineSegment(sketch, "E7.3.0.180", {"start": v(102, 9.55) * mm, "end": v(102, 4.27) * mm, "construction": true});
            skLineSegment(sketch, "E7.3.0.181", {"start": v(42, 9.55) * mm, "end": v(42, 4.27) * mm, "construction": true});
            skLineSegment(sketch, "E7.3.0.182", {"start": v(28, 1) * mm, "end": v(28, -1) * mm});
            skLineSegment(sketch, "E7.3.0.183", {"start": v(92, 6.27) * mm, "end": v(92, 4.27) * mm});
            skLineSegment(sketch, "E7.3.0.184", {"start": v(68, -4.28) * mm, "end": v(68, -6.28) * mm});
            skLineSegment(sketch, "E7.3.0.185", {"start": v(28, 1) * mm, "end": v(32, 1) * mm});
            skLineSegment(sketch, "E7.3.0.186", {"start": v(58, 1) * mm, "end": v(58, -1) * mm});
            skLineSegment(sketch, "E7.3.0.187", {"start": v(42, -4.28) * mm, "end": v(42, -6.28) * mm});
            skLineSegment(sketch, "E7.3.0.188", {"start": v(72, 9.55) * mm, "end": v(72, 4.27) * mm, "construction": true});
            skLineSegment(sketch, "E7.3.0.189", {"start": v(98, -4.28) * mm, "end": v(98, -6.28) * mm});
            skLineSegment(sketch, "E7.3.0.190", {"start": v(98, 4.27) * mm, "end": v(102, 4.27) * mm});
            skLineSegment(sketch, "E7.3.0.191", {"start": v(108, -1) * mm, "end": v(112, -1) * mm});
            skLineSegment(sketch, "E7.3.0.192", {"start": v(102, 6.27) * mm, "end": v(102, 4.27) * mm});
            skLineSegment(sketch, "E7.3.0.193", {"start": v(78, -1) * mm, "end": v(82, -1) * mm});
            skLineSegment(sketch, "E7.3.0.194", {"start": v(68, 4.27) * mm, "end": v(72, 4.27) * mm});
            skLineSegment(sketch, "E7.3.0.195", {"start": v(112, 1) * mm, "end": v(112, -1) * mm});
            skLineSegment(sketch, "E7.3.0.196", {"start": v(72, 6.27) * mm, "end": v(72, 4.27) * mm});
            skLineSegment(sketch, "E7.3.0.197", {"start": v(98, 6.27) * mm, "end": v(102, 6.27) * mm});
            skLineSegment(sketch, "E7.3.0.198", {"start": v(22, 11.55) * mm, "end": v(22, 9.55) * mm});
            skLineSegment(sketch, "E7.3.0.199", {"start": v(22, 1) * mm, "end": v(22, -1) * mm});
            skLineSegment(sketch, "E7.3.0.200", {"start": v(42, 6.27) * mm, "end": v(42, 4.27) * mm});
            skLineSegment(sketch, "E7.3.0.201", {"start": v(68, 6.27) * mm, "end": v(72, 6.27) * mm});
            skLineSegment(sketch, "E7.3.0.202", {"start": v(22, 9.55) * mm, "end": v(22, 4.27) * mm, "construction": true});
            skLineSegment(sketch, "E7.3.0.203", {"start": v(98, 6.27) * mm, "end": v(98, 4.27) * mm});
            skLineSegment(sketch, "E7.3.0.204", {"start": v(82, 1) * mm, "end": v(82, -1) * mm});
            skLineSegment(sketch, "E7.3.0.205", {"start": v(108, 1) * mm, "end": v(112, 1) * mm});
            skLineSegment(sketch, "E7.3.0.206", {"start": v(68, 6.27) * mm, "end": v(68, 4.27) * mm});
            skLineSegment(sketch, "E7.3.0.207", {"start": v(102, 11.55) * mm, "end": v(102, 9.55) * mm});
            skLineSegment(sketch, "E7.3.0.208", {"start": v(92, -4.28) * mm, "end": v(92, -6.28) * mm});
            skLineSegment(sketch, "E7.3.0.209", {"start": v(78, 1) * mm, "end": v(82, 1) * mm});
            skLineSegment(sketch, "E7.3.0.210", {"start": v(108, 1) * mm, "end": v(108, -1) * mm});
            skLineSegment(sketch, "E7.4.0.0", {"start": v(128, -9.55) * mm, "end": v(132, -9.55) * mm});
            skLineSegment(sketch, "E7.4.0.1", {"start": v(132, -9.55) * mm, "end": v(132, -11.55) * mm});
            skLineSegment(sketch, "E7.4.0.2", {"start": v(198, 11.55) * mm, "end": v(198, 9.55) * mm});
            skLineSegment(sketch, "E7.4.0.3", {"start": v(188, -1) * mm, "end": v(192, -1) * mm});
            skLineSegment(sketch, "E7.4.0.4", {"start": v(168, 11.55) * mm, "end": v(168, 9.55) * mm});
            skLineSegment(sketch, "E7.4.0.5", {"start": v(198, 9.55) * mm, "end": v(202, 9.55) * mm});
            skLineSegment(sketch, "E7.4.0.6", {"start": v(138, 11.55) * mm, "end": v(138, 9.55) * mm});
            skLineSegment(sketch, "E7.4.0.7", {"start": v(168, 9.55) * mm, "end": v(172, 9.55) * mm});
            skLineSegment(sketch, "E7.4.0.8", {"start": v(198, -9.55) * mm, "end": v(198, -11.55) * mm});
            skLineSegment(sketch, "E7.4.0.9", {"start": v(138, 9.55) * mm, "end": v(142, 9.55) * mm});
            skLineSegment(sketch, "E7.4.0.10", {"start": v(192, 1) * mm, "end": v(192, -1) * mm});
            skLineSegment(sketch, "E7.4.0.11", {"start": v(208, 6.27) * mm, "end": v(208, 4.27) * mm});
            skLineSegment(sketch, "E7.4.0.12", {"start": v(198, 11.55) * mm, "end": v(202, 11.55) * mm});
            skLineSegment(sketch, "E7.4.0.13", {"start": v(202, -9.55) * mm, "end": v(202, -11.55) * mm});
            skLineSegment(sketch, "E7.4.0.14", {"start": v(128, -11.55) * mm, "end": v(132, -11.55) * mm});
            skLineSegment(sketch, "E7.4.0.15", {"start": v(188, 1) * mm, "end": v(192, 1) * mm});
            skLineSegment(sketch, "E7.4.0.16", {"start": v(168, 11.55) * mm, "end": v(172, 11.55) * mm});
            skLineSegment(sketch, "E7.4.0.17", {"start": v(172, -9.55) * mm, "end": v(172, -11.55) * mm});
            skLineSegment(sketch, "E7.4.0.18", {"start": v(198, -9.55) * mm, "end": v(202, -9.55) * mm});
            skLineSegment(sketch, "E7.4.0.19", {"start": v(138, 11.55) * mm, "end": v(142, 11.55) * mm});
            skLineSegment(sketch, "E7.4.0.20", {"start": v(168, -9.55) * mm, "end": v(172, -9.55) * mm});
            skLineSegment(sketch, "E7.4.0.21", {"start": v(168, -1) * mm, "end": v(172, -1) * mm});
            skLineSegment(sketch, "E7.4.0.22", {"start": v(198, -11.55) * mm, "end": v(202, -11.55) * mm});
            skLineSegment(sketch, "E7.4.0.23", {"start": v(138, -1) * mm, "end": v(142, -1) * mm});
            skLineSegment(sketch, "E7.4.0.24", {"start": v(168, -11.55) * mm, "end": v(172, -11.55) * mm});
            skLineSegment(sketch, "E7.4.0.25", {"start": v(178, -9.55) * mm, "end": v(178, -11.55) * mm});
            skLineSegment(sketch, "E7.4.0.26", {"start": v(212, -9.55) * mm, "end": v(212, -11.55) * mm});
            skLineSegment(sketch, "E7.4.0.27", {"start": v(172, 1) * mm, "end": v(172, -1) * mm});
            skLineSegment(sketch, "E7.4.0.28", {"start": v(148, -9.55) * mm, "end": v(148, -11.55) * mm});
            skLineSegment(sketch, "E7.4.0.29", {"start": v(182, -9.55) * mm, "end": v(182, -11.55) * mm});
            skLineSegment(sketch, "E7.4.0.30", {"start": v(208, -9.55) * mm, "end": v(212, -9.55) * mm});
            skLineSegment(sketch, "E7.4.0.31", {"start": v(168, 1) * mm, "end": v(172, 1) * mm});
            skLineSegment(sketch, "E7.4.0.32", {"start": v(152, -9.55) * mm, "end": v(152, -11.55) * mm});
            skLineSegment(sketch, "E7.4.0.33", {"start": v(178, -9.55) * mm, "end": v(182, -9.55) * mm});
            skLineSegment(sketch, "E7.4.0.34", {"start": v(148, -9.55) * mm, "end": v(152, -9.55) * mm});
            skLineSegment(sketch, "E7.4.0.35", {"start": v(188, 11.55) * mm, "end": v(188, 9.55) * mm});
            skLineSegment(sketch, "E7.4.0.36", {"start": v(128, 6.27) * mm, "end": v(128, 4.27) * mm});
            skLineSegment(sketch, "E7.4.0.37", {"start": v(188, 9.55) * mm, "end": v(192, 9.55) * mm});
            skLineSegment(sketch, "E7.4.0.38", {"start": v(208, -11.55) * mm, "end": v(212, -11.55) * mm});
            skLineSegment(sketch, "E7.4.0.39", {"start": v(138, 1) * mm, "end": v(138, -1) * mm});
            skLineSegment(sketch, "E7.4.0.40", {"start": v(178, -11.55) * mm, "end": v(182, -11.55) * mm});
            skLineSegment(sketch, "E7.4.0.41", {"start": v(118, 11.55) * mm, "end": v(122, 11.55) * mm});
            skLineSegment(sketch, "E7.4.0.42", {"start": v(118, 9.55) * mm, "end": v(122, 9.55) * mm});
            skLineSegment(sketch, "E7.4.0.43", {"start": v(118, 11.55) * mm, "end": v(118, 9.55) * mm});
            skLineSegment(sketch, "E7.4.0.44", {"start": v(118, 6.27) * mm, "end": v(118, 4.27) * mm});
            skLineSegment(sketch, "E7.4.0.45", {"start": v(118, 6.27) * mm, "end": v(122, 6.27) * mm});
            skLineSegment(sketch, "E7.4.0.46", {"start": v(118, 4.27) * mm, "end": v(122, 4.27) * mm});
            skLineSegment(sketch, "E7.4.0.47", {"start": v(148, -11.55) * mm, "end": v(152, -11.55) * mm});
            skLineSegment(sketch, "E7.4.0.48", {"start": v(188, 11.55) * mm, "end": v(192, 11.55) * mm});
            skLineSegment(sketch, "E7.4.0.49", {"start": v(138, 6.27) * mm, "end": v(138, 4.27) * mm});
            skLineSegment(sketch, "E7.4.0.50", {"start": v(128, 11.55) * mm, "end": v(132, 11.55) * mm});
            skLineSegment(sketch, "E7.4.0.51", {"start": v(172, 11.55) * mm, "end": v(172, 9.55) * mm});
            skLineSegment(sketch, "E7.4.0.52", {"start": v(162, -4.28) * mm, "end": v(162, -6.28) * mm});
            skLineSegment(sketch, "E7.4.0.53", {"start": v(158, -9.55) * mm, "end": v(162, -9.55) * mm});
            skLineSegment(sketch, "E7.4.0.54", {"start": v(148, 1) * mm, "end": v(152, 1) * mm});
            skLineSegment(sketch, "E7.4.0.55", {"start": v(188, -4.28) * mm, "end": v(192, -4.28) * mm});
            skLineSegment(sketch, "E7.4.0.56", {"start": v(208, 4.27) * mm, "end": v(212, 4.27) * mm});
            skLineSegment(sketch, "E7.4.0.57", {"start": v(162, 9.55) * mm, "end": v(162, 4.27) * mm, "construction": true});
            skLineSegment(sketch, "E7.4.0.58", {"start": v(148, 1) * mm, "end": v(148, -1) * mm});
            skLineSegment(sketch, "E7.4.0.59", {"start": v(142, 11.55) * mm, "end": v(142, 9.55) * mm});
            skLineSegment(sketch, "E7.4.0.60", {"start": v(132, -4.28) * mm, "end": v(132, -6.28) * mm});
            skLineSegment(sketch, "E7.4.0.61", {"start": v(178, 4.27) * mm, "end": v(182, 4.27) * mm});
            skLineSegment(sketch, "E7.4.0.62", {"start": v(158, -4.28) * mm, "end": v(162, -4.28) * mm});
            skLineSegment(sketch, "E7.4.0.63", {"start": v(212, 6.27) * mm, "end": v(212, 4.27) * mm});
            skLineSegment(sketch, "E7.4.0.64", {"start": v(188, -4.28) * mm, "end": v(188, -6.28) * mm});
            skLineSegment(sketch, "E7.4.0.65", {"start": v(132, 9.55) * mm, "end": v(132, 4.27) * mm, "construction": true});
            skLineSegment(sketch, "E7.4.0.66", {"start": v(158, -1) * mm, "end": v(162, -1) * mm});
            skLineSegment(sketch, "E7.4.0.67", {"start": v(148, 4.27) * mm, "end": v(152, 4.27) * mm});
            skLineSegment(sketch, "E7.4.0.68", {"start": v(128, -4.28) * mm, "end": v(132, -4.28) * mm});
            skLineSegment(sketch, "E7.4.0.69", {"start": v(188, -11.55) * mm, "end": v(192, -11.55) * mm});
            skLineSegment(sketch, "E7.4.0.70", {"start": v(182, 6.27) * mm, "end": v(182, 4.27) * mm});
            skLineSegment(sketch, "E7.4.0.71", {"start": v(208, 6.27) * mm, "end": v(212, 6.27) * mm});
            skLineSegment(sketch, "E7.4.0.72", {"start": v(198, -6.28) * mm, "end": v(202, -6.28) * mm});
            skLineSegment(sketch, "E7.4.0.73", {"start": v(158, -11.55) * mm, "end": v(162, -11.55) * mm});
            skLineSegment(sketch, "E7.4.0.74", {"start": v(152, 6.27) * mm, "end": v(152, 4.27) * mm});
            skLineSegment(sketch, "E7.4.0.75", {"start": v(178, 6.27) * mm, "end": v(182, 6.27) * mm});
            skLineSegment(sketch, "E7.4.0.76", {"start": v(168, -6.28) * mm, "end": v(172, -6.28) * mm});
            skLineSegment(sketch, "E7.4.0.77", {"start": v(168, -9.55) * mm, "end": v(168, -11.55) * mm});
            skLineSegment(sketch, "E7.4.0.78", {"start": v(162, 1) * mm, "end": v(162, -1) * mm});
            skLineSegment(sketch, "E7.4.0.79", {"start": v(148, 6.27) * mm, "end": v(152, 6.27) * mm});
            skLineSegment(sketch, "E7.4.0.80", {"start": v(138, -6.28) * mm, "end": v(142, -6.28) * mm});
            skLineSegment(sketch, "E7.4.0.81", {"start": v(138, -9.55) * mm, "end": v(138, -11.55) * mm});
            skLineSegment(sketch, "E7.4.0.82", {"start": v(178, 6.27) * mm, "end": v(178, 4.27) * mm});
            skLineSegment(sketch, "E7.4.0.83", {"start": v(212, 11.55) * mm, "end": v(212, 9.55) * mm});
            skLineSegment(sketch, "E7.4.0.84", {"start": v(202, -4.28) * mm, "end": v(202, -6.28) * mm});
            skLineSegment(sketch, "E7.4.0.85", {"start": v(158, 1) * mm, "end": v(162, 1) * mm});
            skLineSegment(sketch, "E7.4.0.86", {"start": v(148, 6.27) * mm, "end": v(148, 4.27) * mm});
            skLineSegment(sketch, "E7.4.0.87", {"start": v(142, -9.55) * mm, "end": v(142, -11.55) * mm});
            skLineSegment(sketch, "E7.4.0.88", {"start": v(188, 1) * mm, "end": v(188, -1) * mm});
            skLineSegment(sketch, "E7.4.0.89", {"start": v(182, 11.55) * mm, "end": v(182, 9.55) * mm});
            skLineSegment(sketch, "E7.4.0.90", {"start": v(172, -4.28) * mm, "end": v(172, -6.28) * mm});
            skLineSegment(sketch, "E7.4.0.91", {"start": v(208, 11.55) * mm, "end": v(208, 9.55) * mm});
            skLineSegment(sketch, "E7.4.0.92", {"start": v(198, -4.28) * mm, "end": v(202, -4.28) * mm});
            skLineSegment(sketch, "E7.4.0.93", {"start": v(158, 4.27) * mm, "end": v(162, 4.27) * mm});
            skLineSegment(sketch, "E7.4.0.94", {"start": v(148, 11.55) * mm, "end": v(148, 9.55) * mm});
            skLineSegment(sketch, "E7.4.0.95", {"start": v(138, -4.28) * mm, "end": v(142, -4.28) * mm});
            skLineSegment(sketch, "E7.4.0.96", {"start": v(178, 9.55) * mm, "end": v(182, 9.55) * mm});
            skLineSegment(sketch, "E7.4.0.97", {"start": v(208, -6.28) * mm, "end": v(212, -6.28) * mm});
            skLineSegment(sketch, "E7.4.0.98", {"start": v(208, -9.55) * mm, "end": v(208, -11.55) * mm});
            skLineSegment(sketch, "E7.4.0.99", {"start": v(152, 11.55) * mm, "end": v(152, 9.55) * mm});
            skLineSegment(sketch, "E7.4.0.100", {"start": v(138, -9.55) * mm, "end": v(142, -9.55) * mm});
            skLineSegment(sketch, "E7.4.0.101", {"start": v(188, 4.27) * mm, "end": v(192, 4.27) * mm});
            skLineSegment(sketch, "E7.4.0.102", {"start": v(178, 11.55) * mm, "end": v(178, 9.55) * mm});
            skLineSegment(sketch, "E7.4.0.103", {"start": v(168, -4.28) * mm, "end": v(172, -4.28) * mm});
            skLineSegment(sketch, "E7.4.0.104", {"start": v(208, 9.55) * mm, "end": v(212, 9.55) * mm});
            skLineSegment(sketch, "E7.4.0.105", {"start": v(198, -1) * mm, "end": v(202, -1) * mm});
            skLineSegment(sketch, "E7.4.0.106", {"start": v(128, 4.27) * mm, "end": v(132, 4.27) * mm});
            skLineSegment(sketch, "E7.4.0.107", {"start": v(162, 6.27) * mm, "end": v(162, 4.27) * mm});
            skLineSegment(sketch, "E7.4.0.108", {"start": v(148, 9.55) * mm, "end": v(152, 9.55) * mm});
            skLineSegment(sketch, "E7.4.0.109", {"start": v(138, -4.28) * mm, "end": v(138, -6.28) * mm});
            skLineSegment(sketch, "E7.4.0.110", {"start": v(202, 1) * mm, "end": v(202, -1) * mm});
            skLineSegment(sketch, "E7.4.0.111", {"start": v(188, 6.27) * mm, "end": v(192, 6.27) * mm});
            skLineSegment(sketch, "E7.4.0.112", {"start": v(178, -6.28) * mm, "end": v(182, -6.28) * mm});
            skLineSegment(sketch, "E7.4.0.113", {"start": v(208, 11.55) * mm, "end": v(212, 11.55) * mm});
            skLineSegment(sketch, "E7.4.0.114", {"start": v(138, -11.55) * mm, "end": v(142, -11.55) * mm});
            skLineSegment(sketch, "E7.4.0.115", {"start": v(132, 6.27) * mm, "end": v(132, 4.27) * mm});
            skLineSegment(sketch, "E7.4.0.116", {"start": v(158, 6.27) * mm, "end": v(162, 6.27) * mm});
            skLineSegment(sketch, "E7.4.0.117", {"start": v(148, -6.28) * mm, "end": v(152, -6.28) * mm});
            skLineSegment(sketch, "E7.4.0.118", {"start": v(198, 1) * mm, "end": v(202, 1) * mm});
            skLineSegment(sketch, "E7.4.0.119", {"start": v(188, 6.27) * mm, "end": v(188, 4.27) * mm});
            skLineSegment(sketch, "E7.4.0.120", {"start": v(178, 11.55) * mm, "end": v(182, 11.55) * mm});
            skLineSegment(sketch, "E7.4.0.121", {"start": v(212, -4.28) * mm, "end": v(212, -6.28) * mm});
            skLineSegment(sketch, "E7.4.0.122", {"start": v(142, 1) * mm, "end": v(142, -1) * mm});
            skLineSegment(sketch, "E7.4.0.123", {"start": v(128, 6.27) * mm, "end": v(132, 6.27) * mm});
            skLineSegment(sketch, "E7.4.0.124", {"start": v(118, -6.28) * mm, "end": v(122, -6.28) * mm});
            skLineSegment(sketch, "E7.4.0.125", {"start": v(158, 6.27) * mm, "end": v(158, 4.27) * mm});
            skLineSegment(sketch, "E7.4.0.126", {"start": v(148, 11.55) * mm, "end": v(152, 11.55) * mm});
            skLineSegment(sketch, "E7.4.0.127", {"start": v(198, 1) * mm, "end": v(198, -1) * mm});
            skLineSegment(sketch, "E7.4.0.128", {"start": v(192, 11.55) * mm, "end": v(192, 9.55) * mm});
            skLineSegment(sketch, "E7.4.0.129", {"start": v(182, -4.28) * mm, "end": v(182, -6.28) * mm});
            skLineSegment(sketch, "E7.4.0.130", {"start": v(208, -4.28) * mm, "end": v(212, -4.28) * mm});
            skLineSegment(sketch, "E7.4.0.131", {"start": v(212, 9.55) * mm, "end": v(212, 4.27) * mm, "construction": true});
            skLineSegment(sketch, "E7.4.0.132", {"start": v(168, 1) * mm, "end": v(168, -1) * mm});
            skLineSegment(sketch, "E7.4.0.133", {"start": v(162, 11.55) * mm, "end": v(162, 9.55) * mm});
            skLineSegment(sketch, "E7.4.0.134", {"start": v(152, -4.28) * mm, "end": v(152, -6.28) * mm});
            skLineSegment(sketch, "E7.4.0.135", {"start": v(178, -4.28) * mm, "end": v(182, -4.28) * mm});
            skLineSegment(sketch, "E7.4.0.136", {"start": v(182, 9.55) * mm, "end": v(182, 4.27) * mm, "construction": true});
            skLineSegment(sketch, "E7.4.0.137", {"start": v(208, -4.28) * mm, "end": v(208, -6.28) * mm});
            skLineSegment(sketch, "E7.4.0.138", {"start": v(138, 1) * mm, "end": v(142, 1) * mm});
            skLineSegment(sketch, "E7.4.0.139", {"start": v(118, -9.55) * mm, "end": v(118, -11.55) * mm});
            skLineSegment(sketch, "E7.4.0.140", {"start": v(178, -4.28) * mm, "end": v(178, -6.28) * mm});
            skLineSegment(sketch, "E7.4.0.141", {"start": v(118, -11.55) * mm, "end": v(128, -11.55) * mm, "construction": true});
            skLineSegment(sketch, "E7.4.0.142", {"start": v(132, 11.55) * mm, "end": v(132, 9.55) * mm});
            skLineSegment(sketch, "E7.4.0.143", {"start": v(118, -9.55) * mm, "end": v(122, -9.55) * mm});
            skLineSegment(sketch, "E7.4.0.144", {"start": v(158, 11.55) * mm, "end": v(158, 9.55) * mm});
            skLineSegment(sketch, "E7.4.0.145", {"start": v(148, -4.28) * mm, "end": v(152, -4.28) * mm});
            skLineSegment(sketch, "E7.4.0.146", {"start": v(152, 9.55) * mm, "end": v(152, 4.27) * mm, "construction": true});
            skLineSegment(sketch, "E7.4.0.147", {"start": v(138, 4.27) * mm, "end": v(142, 4.27) * mm});
            skLineSegment(sketch, "E7.4.0.148", {"start": v(128, 11.55) * mm, "end": v(128, 9.55) * mm});
            skLineSegment(sketch, "E7.4.0.149", {"start": v(122, -9.55) * mm, "end": v(122, -11.55) * mm});
            skLineSegment(sketch, "E7.4.0.150", {"start": v(158, 9.55) * mm, "end": v(162, 9.55) * mm});
            skLineSegment(sketch, "E7.4.0.151", {"start": v(148, -4.28) * mm, "end": v(148, -6.28) * mm});
            skLineSegment(sketch, "E7.4.0.152", {"start": v(148, -1) * mm, "end": v(152, -1) * mm});
            skLineSegment(sketch, "E7.4.0.153", {"start": v(188, -6.28) * mm, "end": v(192, -6.28) * mm});
            skLineSegment(sketch, "E7.4.0.154", {"start": v(188, -9.55) * mm, "end": v(188, -11.55) * mm});
            skLineSegment(sketch, "E7.4.0.155", {"start": v(118, -4.28) * mm, "end": v(118, -6.28) * mm});
            skLineSegment(sketch, "E7.4.0.156", {"start": v(118, -4.28) * mm, "end": v(122, -4.28) * mm});
            skLineSegment(sketch, "E7.4.0.157", {"start": v(122, -4.28) * mm, "end": v(122, -6.28) * mm});
            skLineSegment(sketch, "E7.4.0.158", {"start": v(122, 6.27) * mm, "end": v(122, 4.27) * mm});
            skLineSegment(sketch, "E7.4.0.159", {"start": v(118, 1) * mm, "end": v(118, -1) * mm});
            skLineSegment(sketch, "E7.4.0.160", {"start": v(118, 1) * mm, "end": v(122, 1) * mm});
            skLineSegment(sketch, "E7.4.0.161", {"start": v(128, 9.55) * mm, "end": v(132, 9.55) * mm});
            skLineSegment(sketch, "E7.4.0.162", {"start": v(118, -11.55) * mm, "end": v(122, -11.55) * mm});
            skLineSegment(sketch, "E7.4.0.163", {"start": v(118, -1) * mm, "end": v(122, -1) * mm});
            skLineSegment(sketch, "E7.4.0.164", {"start": v(158, -6.28) * mm, "end": v(162, -6.28) * mm});
            skLineSegment(sketch, "E7.4.0.165", {"start": v(158, -9.55) * mm, "end": v(158, -11.55) * mm});
            skLineSegment(sketch, "E7.4.0.166", {"start": v(192, -9.55) * mm, "end": v(192, -11.55) * mm});
            skLineSegment(sketch, "E7.4.0.167", {"start": v(138, 6.27) * mm, "end": v(142, 6.27) * mm});
            skLineSegment(sketch, "E7.4.0.168", {"start": v(128, -6.28) * mm, "end": v(132, -6.28) * mm});
            skLineSegment(sketch, "E7.4.0.169", {"start": v(128, -9.55) * mm, "end": v(128, -11.55) * mm});
            skLineSegment(sketch, "E7.4.0.170", {"start": v(158, 11.55) * mm, "end": v(162, 11.55) * mm});
            skLineSegment(sketch, "E7.4.0.171", {"start": v(162, -9.55) * mm, "end": v(162, -11.55) * mm});
            skLineSegment(sketch, "E7.4.0.172", {"start": v(152, 1) * mm, "end": v(152, -1) * mm});
            skLineSegment(sketch, "E7.4.0.173", {"start": v(188, -9.55) * mm, "end": v(192, -9.55) * mm});
            skLineSegment(sketch, "E7.4.0.174", {"start": v(192, 9.55) * mm, "end": v(192, 4.27) * mm, "construction": true});
            skLineSegment(sketch, "E7.4.0.175", {"start": v(178, 1) * mm, "end": v(178, -1) * mm});
            skLineSegment(sketch, "E7.4.0.176", {"start": v(158, -4.28) * mm, "end": v(158, -6.28) * mm});
            skLineSegment(sketch, "E7.4.0.177", {"start": v(128, -1) * mm, "end": v(132, -1) * mm});
            skLineSegment(sketch, "E7.4.0.178", {"start": v(128, -4.28) * mm, "end": v(128, -6.28) * mm});
            skLineSegment(sketch, "E7.4.0.179", {"start": v(132, 1) * mm, "end": v(132, -1) * mm});
            skLineSegment(sketch, "E7.4.0.180", {"start": v(202, 9.55) * mm, "end": v(202, 4.27) * mm, "construction": true});
            skLineSegment(sketch, "E7.4.0.181", {"start": v(142, 9.55) * mm, "end": v(142, 4.27) * mm, "construction": true});
            skLineSegment(sketch, "E7.4.0.182", {"start": v(128, 1) * mm, "end": v(128, -1) * mm});
            skLineSegment(sketch, "E7.4.0.183", {"start": v(192, 6.27) * mm, "end": v(192, 4.27) * mm});
            skLineSegment(sketch, "E7.4.0.184", {"start": v(168, -4.28) * mm, "end": v(168, -6.28) * mm});
            skLineSegment(sketch, "E7.4.0.185", {"start": v(128, 1) * mm, "end": v(132, 1) * mm});
            skLineSegment(sketch, "E7.4.0.186", {"start": v(158, 1) * mm, "end": v(158, -1) * mm});
            skLineSegment(sketch, "E7.4.0.187", {"start": v(142, -4.28) * mm, "end": v(142, -6.28) * mm});
            skLineSegment(sketch, "E7.4.0.188", {"start": v(172, 9.55) * mm, "end": v(172, 4.27) * mm, "construction": true});
            skLineSegment(sketch, "E7.4.0.189", {"start": v(198, -4.28) * mm, "end": v(198, -6.28) * mm});
            skLineSegment(sketch, "E7.4.0.190", {"start": v(198, 4.27) * mm, "end": v(202, 4.27) * mm});
            skLineSegment(sketch, "E7.4.0.191", {"start": v(208, -1) * mm, "end": v(212, -1) * mm});
            skLineSegment(sketch, "E7.4.0.192", {"start": v(202, 6.27) * mm, "end": v(202, 4.27) * mm});
            skLineSegment(sketch, "E7.4.0.193", {"start": v(178, -1) * mm, "end": v(182, -1) * mm});
            skLineSegment(sketch, "E7.4.0.194", {"start": v(168, 4.27) * mm, "end": v(172, 4.27) * mm});
            skLineSegment(sketch, "E7.4.0.195", {"start": v(212, 1) * mm, "end": v(212, -1) * mm});
            skLineSegment(sketch, "E7.4.0.196", {"start": v(172, 6.27) * mm, "end": v(172, 4.27) * mm});
            skLineSegment(sketch, "E7.4.0.197", {"start": v(198, 6.27) * mm, "end": v(202, 6.27) * mm});
            skLineSegment(sketch, "E7.4.0.198", {"start": v(122, 11.55) * mm, "end": v(122, 9.55) * mm});
            skLineSegment(sketch, "E7.4.0.199", {"start": v(122, 1) * mm, "end": v(122, -1) * mm});
            skLineSegment(sketch, "E7.4.0.200", {"start": v(142, 6.27) * mm, "end": v(142, 4.27) * mm});
            skLineSegment(sketch, "E7.4.0.201", {"start": v(168, 6.27) * mm, "end": v(172, 6.27) * mm});
            skLineSegment(sketch, "E7.4.0.202", {"start": v(122, 9.55) * mm, "end": v(122, 4.27) * mm, "construction": true});
            skLineSegment(sketch, "E7.4.0.203", {"start": v(198, 6.27) * mm, "end": v(198, 4.27) * mm});
            skLineSegment(sketch, "E7.4.0.204", {"start": v(182, 1) * mm, "end": v(182, -1) * mm});
            skLineSegment(sketch, "E7.4.0.205", {"start": v(208, 1) * mm, "end": v(212, 1) * mm});
            skLineSegment(sketch, "E7.4.0.206", {"start": v(168, 6.27) * mm, "end": v(168, 4.27) * mm});
            skLineSegment(sketch, "E7.4.0.207", {"start": v(202, 11.55) * mm, "end": v(202, 9.55) * mm});
            skLineSegment(sketch, "E7.4.0.208", {"start": v(192, -4.28) * mm, "end": v(192, -6.28) * mm});
            skLineSegment(sketch, "E7.4.0.209", {"start": v(178, 1) * mm, "end": v(182, 1) * mm});
            skLineSegment(sketch, "E7.4.0.210", {"start": v(208, 1) * mm, "end": v(208, -1) * mm});
            skLineSegment(sketch, "E7.5.0.0", {"start": v(228, -9.55) * mm, "end": v(232, -9.55) * mm});
            skLineSegment(sketch, "E7.5.0.1", {"start": v(232, -9.55) * mm, "end": v(232, -11.55) * mm});
            skLineSegment(sketch, "E7.5.0.4", {"start": v(268, 11.55) * mm, "end": v(268, 9.55) * mm});
            skLineSegment(sketch, "E7.5.0.6", {"start": v(238, 11.55) * mm, "end": v(238, 9.55) * mm});
            skLineSegment(sketch, "E7.5.0.7", {"start": v(268, 9.55) * mm, "end": v(272, 9.55) * mm});
            skLineSegment(sketch, "E7.5.0.9", {"start": v(238, 9.55) * mm, "end": v(242, 9.55) * mm});
            skLineSegment(sketch, "E7.5.0.14", {"start": v(228, -11.55) * mm, "end": v(232, -11.55) * mm});
            skLineSegment(sketch, "E7.5.0.16", {"start": v(268, 11.55) * mm, "end": v(272, 11.55) * mm});
            skLineSegment(sketch, "E7.5.0.17", {"start": v(272, -9.55) * mm, "end": v(272, -11.55) * mm});
            skLineSegment(sketch, "E7.5.0.19", {"start": v(238, 11.55) * mm, "end": v(242, 11.55) * mm});
            skLineSegment(sketch, "E7.5.0.20", {"start": v(268, -9.55) * mm, "end": v(272, -9.55) * mm});
            skLineSegment(sketch, "E7.5.0.21", {"start": v(268, -1) * mm, "end": v(272, -1) * mm});
            skLineSegment(sketch, "E7.5.0.23", {"start": v(238, -1) * mm, "end": v(242, -1) * mm});
            skLineSegment(sketch, "E7.5.0.24", {"start": v(268, -11.55) * mm, "end": v(272, -11.55) * mm});
            skLineSegment(sketch, "E7.5.0.25", {"start": v(278, -9.55) * mm, "end": v(278, -11.55) * mm});
            skLineSegment(sketch, "E7.5.0.27", {"start": v(272, 1) * mm, "end": v(272, -1) * mm});
            skLineSegment(sketch, "E7.5.0.28", {"start": v(248, -9.55) * mm, "end": v(248, -11.55) * mm});
            skLineSegment(sketch, "E7.5.0.29", {"start": v(282, -9.55) * mm, "end": v(282, -11.55) * mm});
            skLineSegment(sketch, "E7.5.0.31", {"start": v(268, 1) * mm, "end": v(272, 1) * mm});
            skLineSegment(sketch, "E7.5.0.32", {"start": v(252, -9.55) * mm, "end": v(252, -11.55) * mm});
            skLineSegment(sketch, "E7.5.0.33", {"start": v(278, -9.55) * mm, "end": v(282, -9.55) * mm});
            skLineSegment(sketch, "E7.5.0.34", {"start": v(248, -9.55) * mm, "end": v(252, -9.55) * mm});
            skLineSegment(sketch, "E7.5.0.36", {"start": v(228, 6.27) * mm, "end": v(228, 4.27) * mm});
            skLineSegment(sketch, "E7.5.0.39", {"start": v(238, 1) * mm, "end": v(238, -1) * mm});
            skLineSegment(sketch, "E7.5.0.40", {"start": v(278, -11.55) * mm, "end": v(282, -11.55) * mm});
            skLineSegment(sketch, "E7.5.0.41", {"start": v(218, 11.55) * mm, "end": v(222, 11.55) * mm});
            skLineSegment(sketch, "E7.5.0.42", {"start": v(218, 9.55) * mm, "end": v(222, 9.55) * mm});
            skLineSegment(sketch, "E7.5.0.43", {"start": v(218, 11.55) * mm, "end": v(218, 9.55) * mm});
            skLineSegment(sketch, "E7.5.0.44", {"start": v(218, 6.27) * mm, "end": v(218, 4.27) * mm});
            skLineSegment(sketch, "E7.5.0.45", {"start": v(218, 6.27) * mm, "end": v(222, 6.27) * mm});
            skLineSegment(sketch, "E7.5.0.46", {"start": v(218, 4.27) * mm, "end": v(222, 4.27) * mm});
            skLineSegment(sketch, "E7.5.0.47", {"start": v(248, -11.55) * mm, "end": v(252, -11.55) * mm});
            skLineSegment(sketch, "E7.5.0.49", {"start": v(238, 6.27) * mm, "end": v(238, 4.27) * mm});
            skLineSegment(sketch, "E7.5.0.50", {"start": v(228, 11.55) * mm, "end": v(232, 11.55) * mm});
            skLineSegment(sketch, "E7.5.0.51", {"start": v(272, 11.55) * mm, "end": v(272, 9.55) * mm});
            skLineSegment(sketch, "E7.5.0.52", {"start": v(262, -4.28) * mm, "end": v(262, -6.28) * mm});
            skLineSegment(sketch, "E7.5.0.53", {"start": v(258, -9.55) * mm, "end": v(262, -9.55) * mm});
            skLineSegment(sketch, "E7.5.0.54", {"start": v(248, 1) * mm, "end": v(252, 1) * mm});
            skLineSegment(sketch, "E7.5.0.57", {"start": v(262, 9.55) * mm, "end": v(262, 4.27) * mm, "construction": true});
            skLineSegment(sketch, "E7.5.0.58", {"start": v(248, 1) * mm, "end": v(248, -1) * mm});
            skLineSegment(sketch, "E7.5.0.59", {"start": v(242, 11.55) * mm, "end": v(242, 9.55) * mm});
            skLineSegment(sketch, "E7.5.0.60", {"start": v(232, -4.28) * mm, "end": v(232, -6.28) * mm});
            skLineSegment(sketch, "E7.5.0.61", {"start": v(278, 4.27) * mm, "end": v(282, 4.27) * mm});
            skLineSegment(sketch, "E7.5.0.62", {"start": v(258, -4.28) * mm, "end": v(262, -4.28) * mm});
            skLineSegment(sketch, "E7.5.0.65", {"start": v(232, 9.55) * mm, "end": v(232, 4.27) * mm, "construction": true});
            skLineSegment(sketch, "E7.5.0.66", {"start": v(258, -1) * mm, "end": v(262, -1) * mm});
            skLineSegment(sketch, "E7.5.0.67", {"start": v(248, 4.27) * mm, "end": v(252, 4.27) * mm});
            skLineSegment(sketch, "E7.5.0.68", {"start": v(228, -4.28) * mm, "end": v(232, -4.28) * mm});
            skLineSegment(sketch, "E7.5.0.70", {"start": v(282, 6.27) * mm, "end": v(282, 4.27) * mm});
            skLineSegment(sketch, "E7.5.0.73", {"start": v(258, -11.55) * mm, "end": v(262, -11.55) * mm});
            skLineSegment(sketch, "E7.5.0.74", {"start": v(252, 6.27) * mm, "end": v(252, 4.27) * mm});
            skLineSegment(sketch, "E7.5.0.75", {"start": v(278, 6.27) * mm, "end": v(282, 6.27) * mm});
            skLineSegment(sketch, "E7.5.0.76", {"start": v(268, -6.28) * mm, "end": v(272, -6.28) * mm});
            skLineSegment(sketch, "E7.5.0.77", {"start": v(268, -9.55) * mm, "end": v(268, -11.55) * mm});
            skLineSegment(sketch, "E7.5.0.78", {"start": v(262, 1) * mm, "end": v(262, -1) * mm});
            skLineSegment(sketch, "E7.5.0.79", {"start": v(248, 6.27) * mm, "end": v(252, 6.27) * mm});
            skLineSegment(sketch, "E7.5.0.80", {"start": v(238, -6.28) * mm, "end": v(242, -6.28) * mm});
            skLineSegment(sketch, "E7.5.0.81", {"start": v(238, -9.55) * mm, "end": v(238, -11.55) * mm});
            skLineSegment(sketch, "E7.5.0.82", {"start": v(278, 6.27) * mm, "end": v(278, 4.27) * mm});
            skLineSegment(sketch, "E7.5.0.85", {"start": v(258, 1) * mm, "end": v(262, 1) * mm});
            skLineSegment(sketch, "E7.5.0.86", {"start": v(248, 6.27) * mm, "end": v(248, 4.27) * mm});
            skLineSegment(sketch, "E7.5.0.87", {"start": v(242, -9.55) * mm, "end": v(242, -11.55) * mm});
            skLineSegment(sketch, "E7.5.0.89", {"start": v(282, 11.55) * mm, "end": v(282, 9.55) * mm});
            skLineSegment(sketch, "E7.5.0.90", {"start": v(272, -4.28) * mm, "end": v(272, -6.28) * mm});
            skLineSegment(sketch, "E7.5.0.93", {"start": v(258, 4.27) * mm, "end": v(262, 4.27) * mm});
            skLineSegment(sketch, "E7.5.0.94", {"start": v(248, 11.55) * mm, "end": v(248, 9.55) * mm});
            skLineSegment(sketch, "E7.5.0.95", {"start": v(238, -4.28) * mm, "end": v(242, -4.28) * mm});
            skLineSegment(sketch, "E7.5.0.96", {"start": v(278, 9.55) * mm, "end": v(282, 9.55) * mm});
            skLineSegment(sketch, "E7.5.0.99", {"start": v(252, 11.55) * mm, "end": v(252, 9.55) * mm});
            skLineSegment(sketch, "E7.5.0.100", {"start": v(238, -9.55) * mm, "end": v(242, -9.55) * mm});
            skLineSegment(sketch, "E7.5.0.102", {"start": v(278, 11.55) * mm, "end": v(278, 9.55) * mm});
            skLineSegment(sketch, "E7.5.0.103", {"start": v(268, -4.28) * mm, "end": v(272, -4.28) * mm});
            skLineSegment(sketch, "E7.5.0.106", {"start": v(228, 4.27) * mm, "end": v(232, 4.27) * mm});
            skLineSegment(sketch, "E7.5.0.107", {"start": v(262, 6.27) * mm, "end": v(262, 4.27) * mm});
            skLineSegment(sketch, "E7.5.0.108", {"start": v(248, 9.55) * mm, "end": v(252, 9.55) * mm});
            skLineSegment(sketch, "E7.5.0.109", {"start": v(238, -4.28) * mm, "end": v(238, -6.28) * mm});
            skLineSegment(sketch, "E7.5.0.112", {"start": v(278, -6.28) * mm, "end": v(282, -6.28) * mm});
            skLineSegment(sketch, "E7.5.0.114", {"start": v(238, -11.55) * mm, "end": v(242, -11.55) * mm});
            skLineSegment(sketch, "E7.5.0.115", {"start": v(232, 6.27) * mm, "end": v(232, 4.27) * mm});
            skLineSegment(sketch, "E7.5.0.116", {"start": v(258, 6.27) * mm, "end": v(262, 6.27) * mm});
            skLineSegment(sketch, "E7.5.0.117", {"start": v(248, -6.28) * mm, "end": v(252, -6.28) * mm});
            skLineSegment(sketch, "E7.5.0.120", {"start": v(278, 11.55) * mm, "end": v(282, 11.55) * mm});
            skLineSegment(sketch, "E7.5.0.122", {"start": v(242, 1) * mm, "end": v(242, -1) * mm});
            skLineSegment(sketch, "E7.5.0.123", {"start": v(228, 6.27) * mm, "end": v(232, 6.27) * mm});
            skLineSegment(sketch, "E7.5.0.124", {"start": v(218, -6.28) * mm, "end": v(222, -6.28) * mm});
            skLineSegment(sketch, "E7.5.0.125", {"start": v(258, 6.27) * mm, "end": v(258, 4.27) * mm});
            skLineSegment(sketch, "E7.5.0.126", {"start": v(248, 11.55) * mm, "end": v(252, 11.55) * mm});
            skLineSegment(sketch, "E7.5.0.129", {"start": v(282, -4.28) * mm, "end": v(282, -6.28) * mm});
            skLineSegment(sketch, "E7.5.0.132", {"start": v(268, 1) * mm, "end": v(268, -1) * mm});
            skLineSegment(sketch, "E7.5.0.133", {"start": v(262, 11.55) * mm, "end": v(262, 9.55) * mm});
            skLineSegment(sketch, "E7.5.0.134", {"start": v(252, -4.28) * mm, "end": v(252, -6.28) * mm});
            skLineSegment(sketch, "E7.5.0.135", {"start": v(278, -4.28) * mm, "end": v(282, -4.28) * mm});
            skLineSegment(sketch, "E7.5.0.136", {"start": v(282, 9.55) * mm, "end": v(282, 4.27) * mm, "construction": true});
            skLineSegment(sketch, "E7.5.0.138", {"start": v(238, 1) * mm, "end": v(242, 1) * mm});
            skLineSegment(sketch, "E7.5.0.139", {"start": v(218, -9.55) * mm, "end": v(218, -11.55) * mm});
            skLineSegment(sketch, "E7.5.0.140", {"start": v(278, -4.28) * mm, "end": v(278, -6.28) * mm});
            skLineSegment(sketch, "E7.5.0.141", {"start": v(218, -11.55) * mm, "end": v(228, -11.55) * mm, "construction": true});
            skLineSegment(sketch, "E7.5.0.142", {"start": v(232, 11.55) * mm, "end": v(232, 9.55) * mm});
            skLineSegment(sketch, "E7.5.0.143", {"start": v(218, -9.55) * mm, "end": v(222, -9.55) * mm});
            skLineSegment(sketch, "E7.5.0.144", {"start": v(258, 11.55) * mm, "end": v(258, 9.55) * mm});
            skLineSegment(sketch, "E7.5.0.145", {"start": v(248, -4.28) * mm, "end": v(252, -4.28) * mm});
            skLineSegment(sketch, "E7.5.0.146", {"start": v(252, 9.55) * mm, "end": v(252, 4.27) * mm, "construction": true});
            skLineSegment(sketch, "E7.5.0.147", {"start": v(238, 4.27) * mm, "end": v(242, 4.27) * mm});
            skLineSegment(sketch, "E7.5.0.148", {"start": v(228, 11.55) * mm, "end": v(228, 9.55) * mm});
            skLineSegment(sketch, "E7.5.0.149", {"start": v(222, -9.55) * mm, "end": v(222, -11.55) * mm});
            skLineSegment(sketch, "E7.5.0.150", {"start": v(258, 9.55) * mm, "end": v(262, 9.55) * mm});
            skLineSegment(sketch, "E7.5.0.151", {"start": v(248, -4.28) * mm, "end": v(248, -6.28) * mm});
            skLineSegment(sketch, "E7.5.0.152", {"start": v(248, -1) * mm, "end": v(252, -1) * mm});
            skLineSegment(sketch, "E7.5.0.155", {"start": v(218, -4.28) * mm, "end": v(218, -6.28) * mm});
            skLineSegment(sketch, "E7.5.0.156", {"start": v(218, -4.28) * mm, "end": v(222, -4.28) * mm});
            skLineSegment(sketch, "E7.5.0.157", {"start": v(222, -4.28) * mm, "end": v(222, -6.28) * mm});
            skLineSegment(sketch, "E7.5.0.158", {"start": v(222, 6.27) * mm, "end": v(222, 4.27) * mm});
            skLineSegment(sketch, "E7.5.0.159", {"start": v(218, 1) * mm, "end": v(218, -1) * mm});
            skLineSegment(sketch, "E7.5.0.160", {"start": v(218, 1) * mm, "end": v(222, 1) * mm});
            skLineSegment(sketch, "E7.5.0.161", {"start": v(228, 9.55) * mm, "end": v(232, 9.55) * mm});
            skLineSegment(sketch, "E7.5.0.162", {"start": v(218, -11.55) * mm, "end": v(222, -11.55) * mm});
            skLineSegment(sketch, "E7.5.0.163", {"start": v(218, -1) * mm, "end": v(222, -1) * mm});
            skLineSegment(sketch, "E7.5.0.164", {"start": v(258, -6.28) * mm, "end": v(262, -6.28) * mm});
            skLineSegment(sketch, "E7.5.0.165", {"start": v(258, -9.55) * mm, "end": v(258, -11.55) * mm});
            skLineSegment(sketch, "E7.5.0.167", {"start": v(238, 6.27) * mm, "end": v(242, 6.27) * mm});
            skLineSegment(sketch, "E7.5.0.168", {"start": v(228, -6.28) * mm, "end": v(232, -6.28) * mm});
            skLineSegment(sketch, "E7.5.0.169", {"start": v(228, -9.55) * mm, "end": v(228, -11.55) * mm});
            skLineSegment(sketch, "E7.5.0.170", {"start": v(258, 11.55) * mm, "end": v(262, 11.55) * mm});
            skLineSegment(sketch, "E7.5.0.171", {"start": v(262, -9.55) * mm, "end": v(262, -11.55) * mm});
            skLineSegment(sketch, "E7.5.0.172", {"start": v(252, 1) * mm, "end": v(252, -1) * mm});
            skLineSegment(sketch, "E7.5.0.175", {"start": v(278, 1) * mm, "end": v(278, -1) * mm});
            skLineSegment(sketch, "E7.5.0.176", {"start": v(258, -4.28) * mm, "end": v(258, -6.28) * mm});
            skLineSegment(sketch, "E7.5.0.177", {"start": v(228, -1) * mm, "end": v(232, -1) * mm});
            skLineSegment(sketch, "E7.5.0.178", {"start": v(228, -4.28) * mm, "end": v(228, -6.28) * mm});
            skLineSegment(sketch, "E7.5.0.179", {"start": v(232, 1) * mm, "end": v(232, -1) * mm});
            skLineSegment(sketch, "E7.5.0.181", {"start": v(242, 9.55) * mm, "end": v(242, 4.27) * mm, "construction": true});
            skLineSegment(sketch, "E7.5.0.182", {"start": v(228, 1) * mm, "end": v(228, -1) * mm});
            skLineSegment(sketch, "E7.5.0.184", {"start": v(268, -4.28) * mm, "end": v(268, -6.28) * mm});
            skLineSegment(sketch, "E7.5.0.185", {"start": v(228, 1) * mm, "end": v(232, 1) * mm});
            skLineSegment(sketch, "E7.5.0.186", {"start": v(258, 1) * mm, "end": v(258, -1) * mm});
            skLineSegment(sketch, "E7.5.0.187", {"start": v(242, -4.28) * mm, "end": v(242, -6.28) * mm});
            skLineSegment(sketch, "E7.5.0.188", {"start": v(272, 9.55) * mm, "end": v(272, 4.27) * mm, "construction": true});
            skLineSegment(sketch, "E7.5.0.193", {"start": v(278, -1) * mm, "end": v(282, -1) * mm});
            skLineSegment(sketch, "E7.5.0.194", {"start": v(268, 4.27) * mm, "end": v(272, 4.27) * mm});
            skLineSegment(sketch, "E7.5.0.196", {"start": v(272, 6.27) * mm, "end": v(272, 4.27) * mm});
            skLineSegment(sketch, "E7.5.0.198", {"start": v(222, 11.55) * mm, "end": v(222, 9.55) * mm});
            skLineSegment(sketch, "E7.5.0.199", {"start": v(222, 1) * mm, "end": v(222, -1) * mm});
            skLineSegment(sketch, "E7.5.0.200", {"start": v(242, 6.27) * mm, "end": v(242, 4.27) * mm});
            skLineSegment(sketch, "E7.5.0.201", {"start": v(268, 6.27) * mm, "end": v(272, 6.27) * mm});
            skLineSegment(sketch, "E7.5.0.202", {"start": v(222, 9.55) * mm, "end": v(222, 4.27) * mm, "construction": true});
            skLineSegment(sketch, "E7.5.0.204", {"start": v(282, 1) * mm, "end": v(282, -1) * mm});
            skLineSegment(sketch, "E7.5.0.206", {"start": v(268, 6.27) * mm, "end": v(268, 4.27) * mm});
            skLineSegment(sketch, "E7.5.0.209", {"start": v(278, 1) * mm, "end": v(282, 1) * mm});
            skLineSegment(sketch, "E7.direction1", {"start": v(-272, -9.55) * mm, "end": v(-172, -9.55) * mm, "construction": true});
            skSolve(sketch);
        }
        {
            var Q0;
            Q0=qSketchRegion(id+"F2",true);
            extrude(context, id + "F3", {"entities" : qUnion([Q0]), "operationType" : NewBodyOperationType.ADD, "depth" : 1 * mm});
        }
        {
            var Q0;
            Q0=makeQuery(id+"F1.opExtrude","SWEPT_BODY",BODY,{"disambiguationData":[OSD([sQuery(id+"F0.wireOp",EDGE,"E0"),sQuery(id+"F0.wireOp",EDGE,"E1")])]});
            transform(context, id + "F4", {"entities" : qUnion([Q0]), "transformType" : TransformType.TRANSLATION_3D, "dx" : 0 * mm, "dy" : 0 * mm, "dz" : 0 * mm, "makeCopy" : true});
        }
        {
            var Q0;
            Q0=qCreatedBy(makeId("Right.planeOp"),FACE);
            var sketch = newSketch(context, id + "F5", { "sketchPlane" : qUnion([Q0])});
            skLineSegment(sketch, "E8.bottom", {"start": v(-17.44, -1.07) * mm, "end": v(17.44, -1.07) * mm});
            skLineSegment(sketch, "E8.top", {"start": v(-17.44, -17.83) * mm, "end": v(17.44, -17.83) * mm});
            skLineSegment(sketch, "E8.left", {"start": v(-17.44, -1.07) * mm, "end": v(-17.44, -17.83) * mm});
            skLineSegment(sketch, "E8.right", {"start": v(17.44, -1.07) * mm, "end": v(17.44, -17.83) * mm});
            skLineSegment(sketch, "E9", {"start": v(0, 3.69) * mm, "end": v(0, -20.76) * mm, "construction": true});
            skSolve(sketch);
        }
        {
            var Q0;
            Q0=qSketchRegion(id+"F5",true);
            extrude(context, id + "F6", {"entities" : qUnion([Q0]), "operationType" : NewBodyOperationType.REMOVE, "endBound" : BoundingType.SYMMETRIC, "oppositeDirection" : true, "depth" : 725 * mm});
        }
    });
